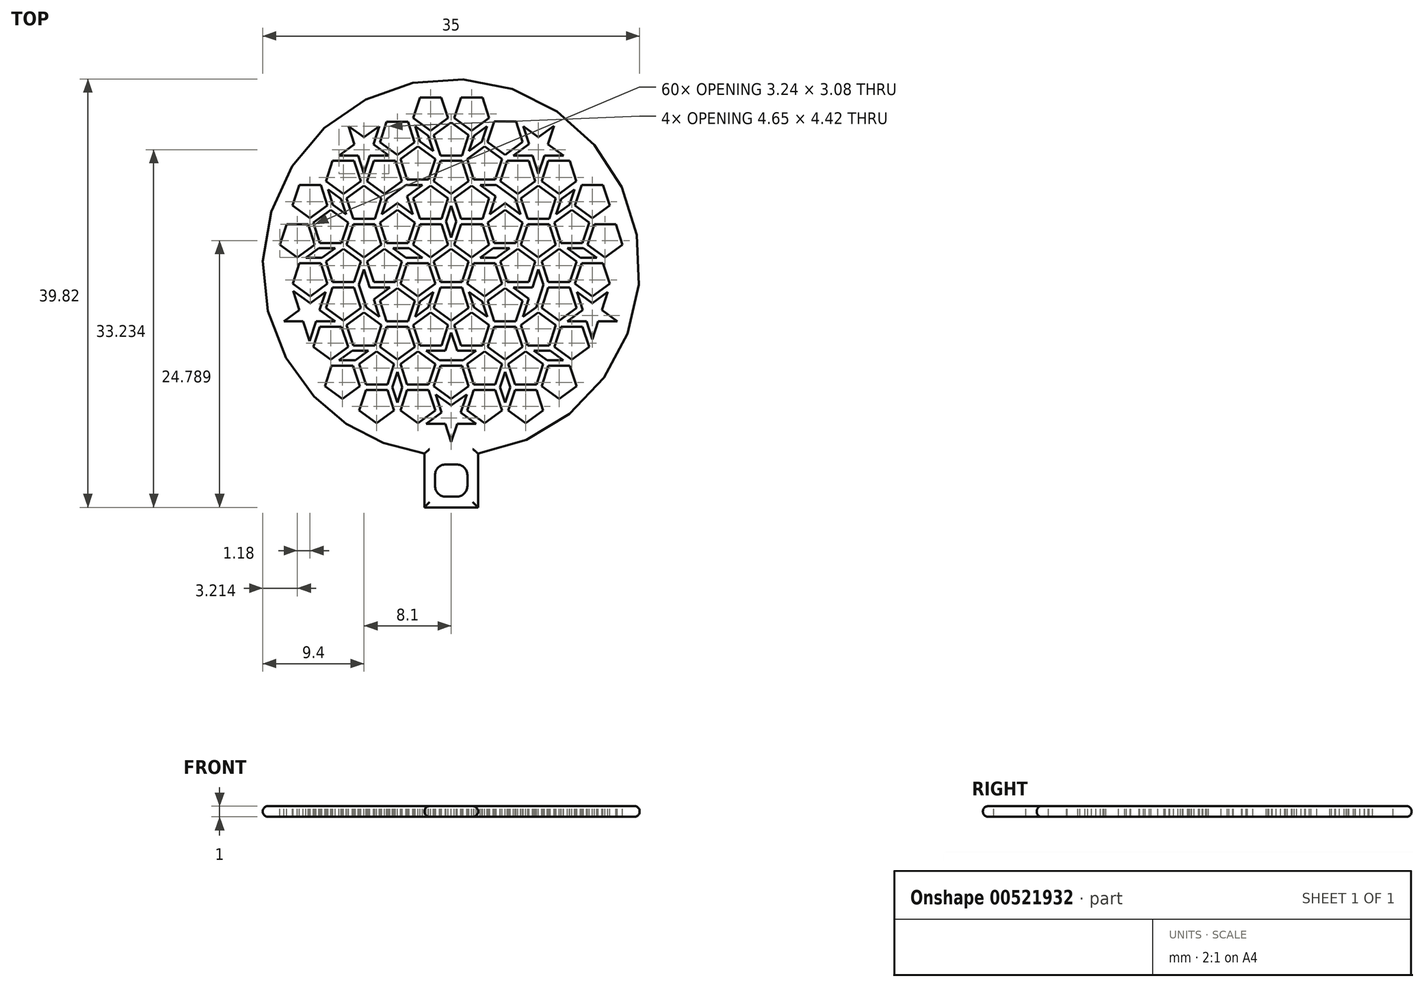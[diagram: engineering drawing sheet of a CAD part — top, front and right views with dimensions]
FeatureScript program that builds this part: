
annotation { "Feature Type Name" : "Feature", "Feature Type Description" : "" }
export const myFeature = defineFeature(function(context is Context, id is Id, definition is map)
    precondition{}
    {
        {
            var Q0;
            Q0=qCreatedBy(makeId("Top.planeOp"),FACE);
            var sketch = newSketch(context, id + "F0", { "sketchPlane" : qUnion([Q0])});
            skArc(sketch, "E0", {"start": v(2.5, -17.32) * mm, "mid": v(0, 17.5) * mm, "end": v(-2.5, -17.32) * mm});
            skLineSegment(sketch, "E1.bottom", {"start": v(2.5, -22.32) * mm, "end": v(-2.5, -22.32) * mm});
            skLineSegment(sketch, "E1.left", {"start": v(2.5, -22.32) * mm, "end": v(2.5, -17.32) * mm});
            skLineSegment(sketch, "E1.right", {"start": v(-2.5, -22.32) * mm, "end": v(-2.5, -17.32) * mm});
            skPoint(sketch, "E1.middle", {"position": v(0, -17.79) * mm});
            skPoint(sketch, "E2.orphan", {"position": v(2.5, -13.25) * mm});
            skPoint(sketch, "E3.orphan", {"position": v(-2.5, -13.25) * mm});
            skSolve(sketch);
        }
        {
            var Q0;
            Q0 = qSketchRegion(id + "F0", true);
            extrude(context, id + "F1", {"entities" : qUnion([Q0]), "depth" : 1 * mm, "offsetDistance" : 25 * mm});
        }
        {
            var Q0;
            Q0=makeQuery(id+"F1.opExtrude","CAP_EDGE",EDGE,{"disambiguationData":[OSD([sQuery(id+"F0.wireOp",EDGE,"E0")])],"isStart":false});
            var Q1;
            Q1=makeQuery(id+"F1.opExtrude","CAP_EDGE",EDGE,{"disambiguationData":[OSD([sQuery(id+"F0.wireOp",EDGE,"E0")])],"isStart":true});
            fillet(context, id + "F2", {"entities" : qUnion([Q0, Q1]), "radius" : 0.5 * mm, "tangentPropagation" : true, "allowEdgeOverflow" : false});
        }
        {
            var Q0;
            Q0=makeQuery(id+"F1.opExtrude","CAP_FACE",FACE,{"disambiguationData":[OSD([sQuery(id+"F0.wireOp",EDGE,"E0")])],"isStart":false});
            var sketch = newSketch(context, id + "F3", { "sketchPlane" : qUnion([Q0])});
            skCircle(sketch, "E4.cCircle", {"center": v(0, 0) * mm, "radius": 1.38 * mm, "construction": true});
            skLineSegment(sketch, "E4.0", {"start": v(0, 1.7) * mm, "end": v(1.62, 0.53) * mm});
            skLineSegment(sketch, "E4.1", {"start": v(1.62, 0.53) * mm, "end": v(1, -1.38) * mm});
            skLineSegment(sketch, "E4.2", {"start": v(1, -1.38) * mm, "end": v(-1, -1.38) * mm});
            skLineSegment(sketch, "E4.3", {"start": v(-1, -1.38) * mm, "end": v(-1.62, 0.53) * mm});
            skLineSegment(sketch, "E4.4", {"start": v(-1.62, 0.53) * mm, "end": v(0, 1.7) * mm});
            skPoint(sketch, "E4.0.midPoint", {"position": v(0.8, 1.11) * mm});
            skCircle(sketch, "E5.cCircle", {"center": v(1.91, 2.63) * mm, "radius": 1.38 * mm, "construction": true});
            skLineSegment(sketch, "E5.0", {"start": v(3.53, 2.1) * mm, "end": v(1.91, 0.93) * mm});
            skLineSegment(sketch, "E5.1", {"start": v(1.91, 0.93) * mm, "end": v(0.3, 2.1) * mm});
            skLineSegment(sketch, "E5.2", {"start": v(0.3, 2.1) * mm, "end": v(0.91, 4) * mm});
            skLineSegment(sketch, "E5.3", {"start": v(0.91, 4) * mm, "end": v(2.91, 4) * mm});
            skLineSegment(sketch, "E5.4", {"start": v(2.91, 4) * mm, "end": v(3.53, 2.1) * mm});
            skPoint(sketch, "E5.0.midPoint", {"position": v(2.72, 1.52) * mm});
            skCircle(sketch, "E6.cCircle", {"center": v(3.1, -1) * mm, "radius": 1.38 * mm, "construction": true});
            skLineSegment(sketch, "E6.0", {"start": v(4.1, 0.37) * mm, "end": v(4.71, -1.53) * mm});
            skLineSegment(sketch, "E6.1", {"start": v(4.71, -1.53) * mm, "end": v(3.1, -2.7) * mm});
            skLineSegment(sketch, "E6.2", {"start": v(3.1, -2.7) * mm, "end": v(1.48, -1.53) * mm});
            skLineSegment(sketch, "E6.3", {"start": v(1.48, -1.53) * mm, "end": v(2.1, 0.37) * mm});
            skLineSegment(sketch, "E6.4", {"start": v(2.1, 0.37) * mm, "end": v(4.1, 0.37) * mm});
            skPoint(sketch, "E6.0.midPoint", {"position": v(4.4, -0.58) * mm});
            skCircle(sketch, "E7.cCircle", {"center": v(0, -3.25) * mm, "radius": 1.38 * mm, "construction": true});
            skLineSegment(sketch, "E7.0", {"start": v(1.62, -3.78) * mm, "end": v(0, -4.95) * mm});
            skLineSegment(sketch, "E7.1", {"start": v(0, -4.95) * mm, "end": v(-1.62, -3.78) * mm});
            skLineSegment(sketch, "E7.2", {"start": v(-1.62, -3.78) * mm, "end": v(-1, -1.88) * mm});
            skLineSegment(sketch, "E7.3", {"start": v(-1, -1.88) * mm, "end": v(1, -1.88) * mm});
            skLineSegment(sketch, "E7.4", {"start": v(1, -1.88) * mm, "end": v(1.62, -3.78) * mm});
            skPoint(sketch, "E7.0.midPoint", {"position": v(0.8, -4.37) * mm});
            skCircle(sketch, "E8.cCircle", {"center": v(-3.1, -1) * mm, "radius": 1.38 * mm, "construction": true});
            skLineSegment(sketch, "E8.0", {"start": v(-4.1, 0.37) * mm, "end": v(-2.1, 0.37) * mm});
            skLineSegment(sketch, "E8.1", {"start": v(-2.1, 0.37) * mm, "end": v(-1.48, -1.53) * mm});
            skLineSegment(sketch, "E8.2", {"start": v(-1.48, -1.53) * mm, "end": v(-3.1, -2.7) * mm});
            skLineSegment(sketch, "E8.3", {"start": v(-3.1, -2.7) * mm, "end": v(-4.71, -1.53) * mm});
            skLineSegment(sketch, "E8.4", {"start": v(-4.71, -1.53) * mm, "end": v(-4.1, 0.37) * mm});
            skPoint(sketch, "E8.0.midPoint", {"position": v(-3.1, 0.37) * mm});
            skCircle(sketch, "E9.cCircle", {"center": v(-1.91, 2.63) * mm, "radius": 1.38 * mm, "construction": true});
            skLineSegment(sketch, "E9.0", {"start": v(-0.91, 4) * mm, "end": v(-0.3, 2.1) * mm});
            skLineSegment(sketch, "E9.1", {"start": v(-0.3, 2.1) * mm, "end": v(-1.91, 0.93) * mm});
            skLineSegment(sketch, "E9.2", {"start": v(-1.91, 0.93) * mm, "end": v(-3.53, 2.1) * mm});
            skLineSegment(sketch, "E9.3", {"start": v(-3.53, 2.1) * mm, "end": v(-2.91, 4) * mm});
            skLineSegment(sketch, "E9.4", {"start": v(-2.91, 4) * mm, "end": v(-0.91, 4) * mm});
            skPoint(sketch, "E9.0.midPoint", {"position": v(-0.6, 3.06) * mm});
            skLineSegment(sketch, "E10.0", {"start": v(5.42, 1.76) * mm, "end": v(4.2, 0.87) * mm});
            skLineSegment(sketch, "E10.1", {"start": v(4.2, 0.87) * mm, "end": v(2.68, 0.87) * mm});
            skLineSegment(sketch, "E10.2", {"start": v(2.68, 0.87) * mm, "end": v(3.9, 1.76) * mm});
            skLineSegment(sketch, "E10.3", {"start": v(3.9, 1.76) * mm, "end": v(5.42, 1.76) * mm});
            skPoint(sketch, "E10.0.midPoint", {"position": v(4.8, 1.32) * mm});
            skLineSegment(sketch, "E11", {"start": v(3.53, 2.1) * mm, "end": v(3.9, 1.76) * mm, "construction": true});
            skLineSegment(sketch, "E12", {"start": v(2.68, 0.87) * mm, "end": v(1.91, 0.93) * mm, "construction": true});
            skLineSegment(sketch, "E13", {"start": v(2.1, 0.37) * mm, "end": v(2.68, 0.87) * mm, "construction": true});
            skLineSegment(sketch, "E14", {"start": v(0.3, 2.1) * mm, "end": v(0, 1.7) * mm, "construction": true});
            skLineSegment(sketch, "E15", {"start": v(1.91, 0.93) * mm, "end": v(1.62, 0.53) * mm, "construction": true});
            skLineSegment(sketch, "E16", {"start": v(1.62, 0.53) * mm, "end": v(2.1, 0.37) * mm, "construction": true});
            skCircle(sketch, "E17.cCircle", {"center": v(5, 3.64) * mm, "radius": 1.38 * mm, "construction": true});
            skLineSegment(sketch, "E17.0", {"start": v(6.62, 4.16) * mm, "end": v(6, 2.26) * mm});
            skLineSegment(sketch, "E17.1", {"start": v(6, 2.26) * mm, "end": v(4, 2.26) * mm});
            skLineSegment(sketch, "E17.2", {"start": v(4, 2.26) * mm, "end": v(3.39, 4.16) * mm});
            skLineSegment(sketch, "E17.3", {"start": v(3.39, 4.16) * mm, "end": v(5, 5.34) * mm});
            skLineSegment(sketch, "E17.4", {"start": v(5, 5.34) * mm, "end": v(6.62, 4.16) * mm});
            skPoint(sketch, "E17.0.midPoint", {"position": v(6.31, 3.21) * mm});
            skLineSegment(sketch, "E18", {"start": v(2.91, 4) * mm, "end": v(3.39, 4.16) * mm, "construction": true});
            skCircle(sketch, "E19.cCircle", {"center": v(6.19, 0) * mm, "radius": 1.38 * mm, "construction": true});
            skLineSegment(sketch, "E19.0", {"start": v(7.8, 0.53) * mm, "end": v(7.19, -1.38) * mm});
            skLineSegment(sketch, "E19.1", {"start": v(7.19, -1.38) * mm, "end": v(5.19, -1.38) * mm});
            skLineSegment(sketch, "E19.2", {"start": v(5.19, -1.38) * mm, "end": v(4.57, 0.53) * mm});
            skLineSegment(sketch, "E19.3", {"start": v(4.57, 0.53) * mm, "end": v(6.19, 1.7) * mm});
            skLineSegment(sketch, "E19.4", {"start": v(6.19, 1.7) * mm, "end": v(7.8, 0.53) * mm});
            skPoint(sketch, "E19.0.midPoint", {"position": v(7.5, -0.43) * mm});
            skLineSegment(sketch, "E20", {"start": v(4.1, 0.37) * mm, "end": v(4.57, 0.53) * mm, "construction": true});
            skLineSegment(sketch, "E21.1", {"start": v(0, 2.75) * mm, "end": v(-0.47, 4.24) * mm});
            skLineSegment(sketch, "E22", {"start": v(-0.47, 4.24) * mm, "end": v(0, 5.7) * mm});
            skLineSegment(sketch, "E23", {"start": v(0, 5.7) * mm, "end": v(0.47, 4.24) * mm});
            skLineSegment(sketch, "E24", {"start": v(-0.3, 2.1) * mm, "end": v(0, 1.7) * mm, "construction": true});
            skLineSegment(sketch, "E25", {"start": v(5.42, 1.76) * mm, "end": v(6, 2.26) * mm, "construction": true});
            skLineSegment(sketch, "E26", {"start": v(5.42, 1.76) * mm, "end": v(6.19, 1.7) * mm, "construction": true});
            skLineSegment(sketch, "E27", {"start": v(0, 2.75) * mm, "end": v(-0.3, 2.1) * mm, "construction": true});
            skLineSegment(sketch, "E28", {"start": v(0.91, 4) * mm, "end": v(0.47, 4.24) * mm, "construction": true});
            skLineSegment(sketch, "E29", {"start": v(-0.47, 4.24) * mm, "end": v(-0.91, 4) * mm, "construction": true});
            skCircle(sketch, "E30.cCircle", {"center": v(1.91, 5.88) * mm, "radius": 1.38 * mm, "construction": true});
            skLineSegment(sketch, "E30.0", {"start": v(2.91, 4.5) * mm, "end": v(0.91, 4.5) * mm});
            skLineSegment(sketch, "E30.1", {"start": v(0.91, 4.5) * mm, "end": v(0.3, 6.41) * mm});
            skLineSegment(sketch, "E30.2", {"start": v(0.3, 6.41) * mm, "end": v(1.91, 7.59) * mm});
            skLineSegment(sketch, "E30.3", {"start": v(1.91, 7.59) * mm, "end": v(3.53, 6.41) * mm});
            skLineSegment(sketch, "E30.4", {"start": v(3.53, 6.41) * mm, "end": v(2.91, 4.5) * mm});
            skPoint(sketch, "E30.0.midPoint", {"position": v(1.91, 4.5) * mm});
            skLineSegment(sketch, "E31", {"start": v(0.91, 4.5) * mm, "end": v(0.91, 4) * mm, "construction": true});
            skLineSegment(sketch, "E32", {"start": v(2.91, 4.5) * mm, "end": v(2.91, 4) * mm, "construction": true});
            skLineSegment(sketch, "E33", {"start": v(0, 5.7) * mm, "end": v(0.3, 6.41) * mm, "construction": true});
            skCircle(sketch, "E34.cCircle", {"center": v(-1.91, 5.88) * mm, "radius": 1.38 * mm, "construction": true});
            skLineSegment(sketch, "E34.0", {"start": v(-0.3, 6.41) * mm, "end": v(-0.91, 4.5) * mm});
            skLineSegment(sketch, "E34.1", {"start": v(-0.91, 4.5) * mm, "end": v(-2.91, 4.5) * mm});
            skLineSegment(sketch, "E34.2", {"start": v(-2.91, 4.5) * mm, "end": v(-3.53, 6.41) * mm});
            skLineSegment(sketch, "E34.3", {"start": v(-3.53, 6.41) * mm, "end": v(-1.91, 7.59) * mm});
            skLineSegment(sketch, "E34.4", {"start": v(-1.91, 7.59) * mm, "end": v(-0.3, 6.41) * mm});
            skPoint(sketch, "E34.0.midPoint", {"position": v(-0.6, 5.46) * mm});
            skLineSegment(sketch, "E35", {"start": v(-0.3, 6.41) * mm, "end": v(0, 5.7) * mm, "construction": true});
            skLineSegment(sketch, "E36", {"start": v(-0.91, 4.5) * mm, "end": v(-0.91, 4) * mm, "construction": true});
            skLineSegment(sketch, "E37", {"start": v(-2.91, 4.5) * mm, "end": v(-2.91, 4) * mm, "construction": true});
            skLineSegment(sketch, "E38", {"start": v(-2.68, 0.87) * mm, "end": v(-3.9, 1.76) * mm});
            skLineSegment(sketch, "E39", {"start": v(-3.9, 1.76) * mm, "end": v(-5.42, 1.76) * mm});
            skLineSegment(sketch, "E40", {"start": v(-5.42, 1.76) * mm, "end": v(-4.2, 0.87) * mm});
            skLineSegment(sketch, "E41", {"start": v(-4.2, 0.87) * mm, "end": v(-2.68, 0.87) * mm});
            skLineSegment(sketch, "E42", {"start": v(-2.68, 0.87) * mm, "end": v(-1.91, 0.93) * mm, "construction": true});
            skLineSegment(sketch, "E43", {"start": v(-2.68, 0.87) * mm, "end": v(-2.1, 0.37) * mm, "construction": true});
            skLineSegment(sketch, "E44", {"start": v(-4.2, 0.87) * mm, "end": v(-4.1, 0.37) * mm, "construction": true});
            skLineSegment(sketch, "E45", {"start": v(-3.9, 1.76) * mm, "end": v(-3.53, 2.1) * mm, "construction": true});
            skLineSegment(sketch, "E46", {"start": v(0, 2.75) * mm, "end": v(0.47, 4.24) * mm});
            skLineSegment(sketch, "E47", {"start": v(0.3, 2.1) * mm, "end": v(0, 2.75) * mm, "construction": true});
            skCircle(sketch, "E48.cCircle", {"center": v(-5, 3.64) * mm, "radius": 1.38 * mm, "construction": true});
            skLineSegment(sketch, "E48.0", {"start": v(-5, 5.34) * mm, "end": v(-3.39, 4.16) * mm});
            skLineSegment(sketch, "E48.1", {"start": v(-3.39, 4.16) * mm, "end": v(-4, 2.26) * mm});
            skLineSegment(sketch, "E48.2", {"start": v(-4, 2.26) * mm, "end": v(-6, 2.26) * mm});
            skLineSegment(sketch, "E48.3", {"start": v(-6, 2.26) * mm, "end": v(-6.62, 4.16) * mm});
            skLineSegment(sketch, "E48.4", {"start": v(-6.62, 4.16) * mm, "end": v(-5, 5.34) * mm});
            skPoint(sketch, "E48.0.midPoint", {"position": v(-4.2, 4.75) * mm});
            skLineSegment(sketch, "E49", {"start": v(-3.39, 4.16) * mm, "end": v(-2.91, 4) * mm, "construction": true});
            skLineSegment(sketch, "E50", {"start": v(-3.53, 2.1) * mm, "end": v(-4, 2.26) * mm, "construction": true});
            skCircle(sketch, "E51.cCircle", {"center": v(-6.19, 0) * mm, "radius": 1.38 * mm, "construction": true});
            skLineSegment(sketch, "E51.0", {"start": v(-6.19, 1.7) * mm, "end": v(-4.57, 0.53) * mm});
            skLineSegment(sketch, "E51.1", {"start": v(-4.57, 0.53) * mm, "end": v(-5.19, -1.38) * mm});
            skLineSegment(sketch, "E51.2", {"start": v(-5.19, -1.38) * mm, "end": v(-7.19, -1.38) * mm});
            skLineSegment(sketch, "E51.3", {"start": v(-7.19, -1.38) * mm, "end": v(-7.8, 0.53) * mm});
            skLineSegment(sketch, "E51.4", {"start": v(-7.8, 0.53) * mm, "end": v(-6.19, 1.7) * mm});
            skPoint(sketch, "E51.0.midPoint", {"position": v(-5.38, 1.11) * mm});
            skLineSegment(sketch, "E52", {"start": v(-4.57, 0.53) * mm, "end": v(-4.1, 0.37) * mm, "construction": true});
            skLineSegment(sketch, "E53", {"start": v(-4.71, -1.53) * mm, "end": v(-5.19, -1.38) * mm, "construction": true});
            skLineSegment(sketch, "E54", {"start": v(-6.19, 1.7) * mm, "end": v(-5.42, 1.76) * mm, "construction": true});
            skLineSegment(sketch, "E55", {"start": v(-6, 2.26) * mm, "end": v(-5.42, 1.76) * mm, "construction": true});
            skLineSegment(sketch, "E56", {"start": v(-2.88, -3.17) * mm, "end": v(-1.66, -2.28) * mm});
            skLineSegment(sketch, "E57", {"start": v(-1.66, -2.28) * mm, "end": v(-2.12, -3.72) * mm});
            skLineSegment(sketch, "E58", {"start": v(-2.12, -3.72) * mm, "end": v(-3.35, -4.6) * mm});
            skLineSegment(sketch, "E59", {"start": v(-3.35, -4.6) * mm, "end": v(-2.88, -3.17) * mm});
            skLineSegment(sketch, "E60", {"start": v(-1.48, -1.53) * mm, "end": v(-1.66, -2.28) * mm, "construction": true});
            skLineSegment(sketch, "E61", {"start": v(-1, -1.88) * mm, "end": v(-1.66, -2.28) * mm, "construction": true});
            skLineSegment(sketch, "E62", {"start": v(-1.62, -3.78) * mm, "end": v(-2.12, -3.72) * mm, "construction": true});
            skLineSegment(sketch, "E63", {"start": v(-2.88, -3.17) * mm, "end": v(-3.1, -2.7) * mm, "construction": true});
            skLineSegment(sketch, "E64", {"start": v(2.12, -3.72) * mm, "end": v(1.66, -2.28) * mm});
            skLineSegment(sketch, "E65", {"start": v(1.66, -2.28) * mm, "end": v(2.88, -3.17) * mm});
            skLineSegment(sketch, "E66", {"start": v(2.88, -3.17) * mm, "end": v(3.35, -4.6) * mm});
            skLineSegment(sketch, "E67", {"start": v(3.35, -4.6) * mm, "end": v(2.12, -3.72) * mm});
            skLineSegment(sketch, "E68", {"start": v(1.66, -2.28) * mm, "end": v(1.48, -1.53) * mm, "construction": true});
            skLineSegment(sketch, "E69", {"start": v(1.66, -2.28) * mm, "end": v(1, -1.88) * mm, "construction": true});
            skCircle(sketch, "E70.cCircle", {"center": v(5, -3.64) * mm, "radius": 1.38 * mm, "construction": true});
            skLineSegment(sketch, "E70.0", {"start": v(6.62, -3.11) * mm, "end": v(6, -5.01) * mm});
            skLineSegment(sketch, "E70.1", {"start": v(6, -5.01) * mm, "end": v(4, -5.01) * mm});
            skLineSegment(sketch, "E70.2", {"start": v(4, -5.01) * mm, "end": v(3.39, -3.11) * mm});
            skLineSegment(sketch, "E70.3", {"start": v(3.39, -3.11) * mm, "end": v(5, -1.94) * mm});
            skLineSegment(sketch, "E70.4", {"start": v(5, -1.94) * mm, "end": v(6.62, -3.11) * mm});
            skPoint(sketch, "E70.0.midPoint", {"position": v(6.31, -4.06) * mm});
            skCircle(sketch, "E71.cCircle", {"center": v(1.91, -5.88) * mm, "radius": 1.38 * mm, "construction": true});
            skLineSegment(sketch, "E71.0", {"start": v(1.91, -4.18) * mm, "end": v(3.53, -5.36) * mm});
            skLineSegment(sketch, "E71.1", {"start": v(3.53, -5.36) * mm, "end": v(2.91, -7.26) * mm});
            skLineSegment(sketch, "E71.2", {"start": v(2.91, -7.26) * mm, "end": v(0.91, -7.26) * mm});
            skLineSegment(sketch, "E71.3", {"start": v(0.91, -7.26) * mm, "end": v(0.3, -5.36) * mm});
            skLineSegment(sketch, "E71.4", {"start": v(0.3, -5.36) * mm, "end": v(1.91, -4.18) * mm});
            skPoint(sketch, "E71.0.midPoint", {"position": v(2.72, -4.77) * mm});
            skCircle(sketch, "E72.cCircle", {"center": v(-1.91, -5.88) * mm, "radius": 1.38 * mm, "construction": true});
            skLineSegment(sketch, "E72.0", {"start": v(-0.3, -5.36) * mm, "end": v(-0.91, -7.26) * mm});
            skLineSegment(sketch, "E72.1", {"start": v(-0.91, -7.26) * mm, "end": v(-2.91, -7.26) * mm});
            skLineSegment(sketch, "E72.2", {"start": v(-2.91, -7.26) * mm, "end": v(-3.53, -5.36) * mm});
            skLineSegment(sketch, "E72.3", {"start": v(-3.53, -5.36) * mm, "end": v(-1.91, -4.18) * mm});
            skLineSegment(sketch, "E72.4", {"start": v(-1.91, -4.18) * mm, "end": v(-0.3, -5.36) * mm});
            skCircle(sketch, "E73.cCircle", {"center": v(-5, -3.64) * mm, "radius": 1.38 * mm, "construction": true});
            skLineSegment(sketch, "E73.0", {"start": v(-3.39, -3.11) * mm, "end": v(-4, -5.01) * mm});
            skLineSegment(sketch, "E73.1", {"start": v(-4, -5.01) * mm, "end": v(-6, -5.01) * mm});
            skLineSegment(sketch, "E73.2", {"start": v(-6, -5.01) * mm, "end": v(-6.62, -3.11) * mm});
            skLineSegment(sketch, "E73.3", {"start": v(-6.62, -3.11) * mm, "end": v(-5, -1.94) * mm});
            skLineSegment(sketch, "E73.4", {"start": v(-5, -1.94) * mm, "end": v(-3.39, -3.11) * mm});
            skPoint(sketch, "E73.0.midPoint", {"position": v(-3.7, -4.06) * mm});
            skLineSegment(sketch, "E74", {"start": v(3.39, -3.11) * mm, "end": v(3.1, -2.7) * mm, "construction": true});
            skLineSegment(sketch, "E75", {"start": v(0.3, -5.36) * mm, "end": v(0, -4.95) * mm, "construction": true});
            skLineSegment(sketch, "E76", {"start": v(-0.3, -5.36) * mm, "end": v(0, -4.95) * mm, "construction": true});
            skLineSegment(sketch, "E77", {"start": v(-5, -1.94) * mm, "end": v(-4.71, -1.53) * mm, "construction": true});
            skLineSegment(sketch, "E78", {"start": v(-3.35, -4.6) * mm, "end": v(-4, -5.01) * mm, "construction": true});
            skLineSegment(sketch, "E79", {"start": v(-3.35, -4.6) * mm, "end": v(-3.53, -5.36) * mm, "construction": true});
            skLineSegment(sketch, "E80", {"start": v(-2.12, -3.72) * mm, "end": v(-1.91, -4.18) * mm, "construction": true});
            skLineSegment(sketch, "E81", {"start": v(-3.39, -3.11) * mm, "end": v(-2.88, -3.17) * mm, "construction": true});
            skLineSegment(sketch, "E82", {"start": v(1.62, -3.78) * mm, "end": v(2.12, -3.72) * mm, "construction": true});
            skLineSegment(sketch, "E83", {"start": v(3.1, -2.7) * mm, "end": v(2.88, -3.17) * mm, "construction": true});
            skLineSegment(sketch, "E84", {"start": v(2.88, -3.17) * mm, "end": v(3.39, -3.11) * mm, "construction": true});
            skLineSegment(sketch, "E85", {"start": v(1.91, -4.18) * mm, "end": v(2.12, -3.72) * mm, "construction": true});
            skCircle(sketch, "E86.cCircle", {"center": v(10.01, 0) * mm, "radius": 1.38 * mm, "construction": true});
            skLineSegment(sketch, "E86.0", {"start": v(11.63, 0.53) * mm, "end": v(11.01, -1.38) * mm});
            skLineSegment(sketch, "E86.1", {"start": v(11.01, -1.38) * mm, "end": v(9.01, -1.38) * mm});
            skLineSegment(sketch, "E86.2", {"start": v(9.01, -1.38) * mm, "end": v(8.4, 0.53) * mm});
            skLineSegment(sketch, "E86.3", {"start": v(8.4, 0.53) * mm, "end": v(10.01, 1.7) * mm});
            skLineSegment(sketch, "E86.4", {"start": v(10.01, 1.7) * mm, "end": v(11.63, 0.53) * mm});
            skPoint(sketch, "E86.0.midPoint", {"position": v(11.32, -0.43) * mm});
            skCircle(sketch, "E87.cCircle", {"center": v(8.1, -5.88) * mm, "radius": 1.38 * mm, "construction": true});
            skLineSegment(sketch, "E87.0", {"start": v(9.1, -7.26) * mm, "end": v(7.1, -7.26) * mm});
            skLineSegment(sketch, "E87.1", {"start": v(7.1, -7.26) * mm, "end": v(6.48, -5.36) * mm});
            skLineSegment(sketch, "E87.2", {"start": v(6.48, -5.36) * mm, "end": v(8.1, -4.18) * mm});
            skLineSegment(sketch, "E87.3", {"start": v(8.1, -4.18) * mm, "end": v(9.72, -5.36) * mm});
            skLineSegment(sketch, "E87.4", {"start": v(9.72, -5.36) * mm, "end": v(9.1, -7.26) * mm});
            skPoint(sketch, "E87.0.midPoint", {"position": v(8.1, -7.26) * mm});
            skCircle(sketch, "E88.cCircle", {"center": v(5, -6.89) * mm, "radius": 1.38 * mm, "construction": true});
            skLineSegment(sketch, "E88.0", {"start": v(6.62, -7.42) * mm, "end": v(5, -8.6) * mm});
            skLineSegment(sketch, "E88.1", {"start": v(5, -8.6) * mm, "end": v(3.39, -7.42) * mm});
            skLineSegment(sketch, "E88.2", {"start": v(3.39, -7.42) * mm, "end": v(4, -5.51) * mm});
            skLineSegment(sketch, "E88.3", {"start": v(4, -5.51) * mm, "end": v(6, -5.51) * mm});
            skLineSegment(sketch, "E88.4", {"start": v(6, -5.51) * mm, "end": v(6.62, -7.42) * mm});
            skPoint(sketch, "E88.0.midPoint", {"position": v(5.81, -8) * mm});
            skCircle(sketch, "E89.cCircle", {"center": v(8.1, 2.63) * mm, "radius": 1.38 * mm, "construction": true});
            skLineSegment(sketch, "E89.0", {"start": v(9.72, 2.1) * mm, "end": v(8.1, 0.93) * mm});
            skLineSegment(sketch, "E89.1", {"start": v(8.1, 0.93) * mm, "end": v(6.48, 2.1) * mm});
            skLineSegment(sketch, "E89.2", {"start": v(6.48, 2.1) * mm, "end": v(7.1, 4) * mm});
            skLineSegment(sketch, "E89.3", {"start": v(7.1, 4) * mm, "end": v(9.1, 4) * mm});
            skLineSegment(sketch, "E89.4", {"start": v(9.1, 4) * mm, "end": v(9.72, 2.1) * mm});
            skPoint(sketch, "E89.0.midPoint", {"position": v(8.9, 1.52) * mm});
            skLineSegment(sketch, "E90", {"start": v(6.48, 2.1) * mm, "end": v(6.19, 1.7) * mm, "construction": true});
            skLineSegment(sketch, "E91", {"start": v(10.01, 1.7) * mm, "end": v(9.72, 2.1) * mm, "construction": true});
            skLineSegment(sketch, "E92", {"start": v(4, -5.51) * mm, "end": v(3.53, -5.36) * mm, "construction": true});
            skLineSegment(sketch, "E93", {"start": v(6.48, -5.36) * mm, "end": v(6, -5.51) * mm, "construction": true});
            skCircle(sketch, "E94.cCircle", {"center": v(10.01, -3.25) * mm, "radius": 1.38 * mm, "construction": true});
            skLineSegment(sketch, "E94.0", {"start": v(11.01, -1.88) * mm, "end": v(11.63, -3.78) * mm});
            skLineSegment(sketch, "E94.1", {"start": v(11.63, -3.78) * mm, "end": v(10.01, -4.95) * mm});
            skLineSegment(sketch, "E94.2", {"start": v(10.01, -4.95) * mm, "end": v(8.4, -3.78) * mm});
            skLineSegment(sketch, "E94.3", {"start": v(8.4, -3.78) * mm, "end": v(9.01, -1.88) * mm});
            skLineSegment(sketch, "E94.4", {"start": v(9.01, -1.88) * mm, "end": v(11.01, -1.88) * mm});
            skPoint(sketch, "E94.0.midPoint", {"position": v(11.32, -2.83) * mm});
            skLineSegment(sketch, "E95", {"start": v(11.01, -1.38) * mm, "end": v(11.01, -1.88) * mm, "construction": true});
            skLineSegment(sketch, "E96", {"start": v(6.66, -4.6) * mm, "end": v(7.21, -2.92) * mm});
            skLineSegment(sketch, "E97", {"start": v(7.21, -2.92) * mm, "end": v(5.77, -1.88) * mm});
            skLineSegment(sketch, "E98", {"start": v(5.77, -1.88) * mm, "end": v(7.55, -1.88) * mm});
            skLineSegment(sketch, "E99", {"start": v(7.55, -1.88) * mm, "end": v(8.1, -0.19) * mm});
            skLineSegment(sketch, "E100", {"start": v(8.1, -0.19) * mm, "end": v(8.57, -1.63) * mm});
            skLineSegment(sketch, "E101", {"start": v(8.57, -1.63) * mm, "end": v(7.89, -3.72) * mm});
            skLineSegment(sketch, "E102", {"start": v(7.89, -3.72) * mm, "end": v(6.66, -4.6) * mm});
            skCircle(sketch, "E103.cCircle", {"center": v(-8.1, 2.63) * mm, "radius": 1.38 * mm, "construction": true});
            skLineSegment(sketch, "E103.0", {"start": v(-6.48, 2.1) * mm, "end": v(-8.1, 0.93) * mm});
            skLineSegment(sketch, "E103.1", {"start": v(-8.1, 0.93) * mm, "end": v(-9.72, 2.1) * mm});
            skLineSegment(sketch, "E103.2", {"start": v(-9.72, 2.1) * mm, "end": v(-9.1, 4) * mm});
            skLineSegment(sketch, "E103.3", {"start": v(-9.1, 4) * mm, "end": v(-7.1, 4) * mm});
            skLineSegment(sketch, "E103.4", {"start": v(-7.1, 4) * mm, "end": v(-6.48, 2.1) * mm});
            skPoint(sketch, "E103.0.midPoint", {"position": v(-7.3, 1.52) * mm});
            skCircle(sketch, "E104.cCircle", {"center": v(0, 8.51) * mm, "radius": 1.38 * mm, "construction": true});
            skLineSegment(sketch, "E104.0", {"start": v(1.62, 7.99) * mm, "end": v(0, 6.81) * mm});
            skLineSegment(sketch, "E104.1", {"start": v(0, 6.81) * mm, "end": v(-1.62, 7.99) * mm});
            skLineSegment(sketch, "E104.2", {"start": v(-1.62, 7.99) * mm, "end": v(-1, 9.9) * mm});
            skLineSegment(sketch, "E104.3", {"start": v(-1, 9.9) * mm, "end": v(1, 9.9) * mm});
            skLineSegment(sketch, "E104.4", {"start": v(1, 9.9) * mm, "end": v(1.62, 7.99) * mm});
            skPoint(sketch, "E104.0.midPoint", {"position": v(0.8, 7.4) * mm});
            skCircle(sketch, "E105.cCircle", {"center": v(3.1, 9.52) * mm, "radius": 1.38 * mm, "construction": true});
            skLineSegment(sketch, "E105.0", {"start": v(4.71, 10.05) * mm, "end": v(4.1, 8.14) * mm});
            skLineSegment(sketch, "E105.1", {"start": v(4.1, 8.14) * mm, "end": v(2.1, 8.14) * mm});
            skLineSegment(sketch, "E105.2", {"start": v(2.1, 8.14) * mm, "end": v(1.47, 10.05) * mm});
            skLineSegment(sketch, "E105.3", {"start": v(1.47, 10.05) * mm, "end": v(3.1, 11.22) * mm});
            skLineSegment(sketch, "E105.4", {"start": v(3.1, 11.22) * mm, "end": v(4.71, 10.05) * mm});
            skPoint(sketch, "E105.0.midPoint", {"position": v(4.4, 9.1) * mm});
            skCircle(sketch, "E106.cCircle", {"center": v(-3.1, 9.52) * mm, "radius": 1.38 * mm, "construction": true});
            skLineSegment(sketch, "E106.0", {"start": v(-2.1, 8.14) * mm, "end": v(-4.1, 8.14) * mm});
            skLineSegment(sketch, "E106.1", {"start": v(-4.1, 8.14) * mm, "end": v(-4.71, 10.05) * mm});
            skLineSegment(sketch, "E106.2", {"start": v(-4.71, 10.05) * mm, "end": v(-3.1, 11.22) * mm});
            skLineSegment(sketch, "E106.3", {"start": v(-3.1, 11.22) * mm, "end": v(-1.48, 10.05) * mm});
            skLineSegment(sketch, "E106.4", {"start": v(-1.48, 10.05) * mm, "end": v(-2.1, 8.14) * mm});
            skPoint(sketch, "E106.0.midPoint", {"position": v(-3.1, 8.14) * mm});
            skCircle(sketch, "E107.cCircle", {"center": v(-8.1, 5.88) * mm, "radius": 1.38 * mm, "construction": true});
            skLineSegment(sketch, "E107.0", {"start": v(-6.48, 6.41) * mm, "end": v(-7.1, 4.5) * mm});
            skLineSegment(sketch, "E107.1", {"start": v(-7.1, 4.5) * mm, "end": v(-9.1, 4.5) * mm});
            skLineSegment(sketch, "E107.2", {"start": v(-9.1, 4.5) * mm, "end": v(-9.72, 6.41) * mm});
            skLineSegment(sketch, "E107.3", {"start": v(-9.72, 6.41) * mm, "end": v(-8.1, 7.59) * mm});
            skLineSegment(sketch, "E107.4", {"start": v(-8.1, 7.59) * mm, "end": v(-6.48, 6.41) * mm});
            skPoint(sketch, "E107.0.midPoint", {"position": v(-6.8, 5.46) * mm});
            skCircle(sketch, "E108.cCircle", {"center": v(-10.01, 0) * mm, "radius": 1.38 * mm, "construction": true});
            skLineSegment(sketch, "E108.0", {"start": v(-8.4, 0.53) * mm, "end": v(-9.01, -1.38) * mm});
            skLineSegment(sketch, "E108.1", {"start": v(-9.01, -1.38) * mm, "end": v(-11.01, -1.38) * mm});
            skLineSegment(sketch, "E108.2", {"start": v(-11.01, -1.38) * mm, "end": v(-11.63, 0.53) * mm});
            skLineSegment(sketch, "E108.3", {"start": v(-11.63, 0.53) * mm, "end": v(-10.01, 1.7) * mm});
            skLineSegment(sketch, "E108.4", {"start": v(-10.01, 1.7) * mm, "end": v(-8.4, 0.53) * mm});
            skPoint(sketch, "E108.0.midPoint", {"position": v(-8.7, -0.43) * mm});
            skLineSegment(sketch, "E109", {"start": v(-6.48, 2.1) * mm, "end": v(-6.19, 1.7) * mm, "construction": true});
            skLineSegment(sketch, "E110", {"start": v(0, 6.81) * mm, "end": v(-0.3, 6.41) * mm, "construction": true});
            skLineSegment(sketch, "E111", {"start": v(-7.1, 4.5) * mm, "end": v(-7.1, 4) * mm, "construction": true});
            skLineSegment(sketch, "E112", {"start": v(-2.1, 8.14) * mm, "end": v(-1.62, 7.99) * mm, "construction": true});
            skLineSegment(sketch, "E113", {"start": v(-8.4, 0.53) * mm, "end": v(-8.1, 0.93) * mm, "construction": true});
            skLineSegment(sketch, "E114", {"start": v(1.62, 7.99) * mm, "end": v(2.1, 8.14) * mm, "construction": true});
            skCircle(sketch, "E115.cCircle", {"center": v(-10.01, -3.25) * mm, "radius": 1.38 * mm, "construction": true});
            skLineSegment(sketch, "E115.0", {"start": v(-9.01, -1.88) * mm, "end": v(-8.4, -3.78) * mm});
            skLineSegment(sketch, "E115.1", {"start": v(-8.4, -3.78) * mm, "end": v(-10.01, -4.95) * mm});
            skLineSegment(sketch, "E115.2", {"start": v(-10.01, -4.95) * mm, "end": v(-11.63, -3.78) * mm});
            skLineSegment(sketch, "E115.3", {"start": v(-11.63, -3.78) * mm, "end": v(-11.01, -1.88) * mm});
            skLineSegment(sketch, "E115.4", {"start": v(-11.01, -1.88) * mm, "end": v(-9.01, -1.88) * mm});
            skPoint(sketch, "E115.0.midPoint", {"position": v(-8.7, -2.83) * mm});
            skCircle(sketch, "E116.cCircle", {"center": v(8.1, 5.88) * mm, "radius": 1.38 * mm, "construction": true});
            skLineSegment(sketch, "E116.0", {"start": v(9.1, 4.5) * mm, "end": v(7.1, 4.5) * mm});
            skLineSegment(sketch, "E116.1", {"start": v(7.1, 4.5) * mm, "end": v(6.48, 6.4) * mm});
            skLineSegment(sketch, "E116.2", {"start": v(6.48, 6.4) * mm, "end": v(8.1, 7.58) * mm});
            skLineSegment(sketch, "E116.3", {"start": v(8.1, 7.58) * mm, "end": v(9.72, 6.4) * mm});
            skLineSegment(sketch, "E116.4", {"start": v(9.72, 6.4) * mm, "end": v(9.1, 4.5) * mm});
            skPoint(sketch, "E116.0.midPoint", {"position": v(8.1, 4.5) * mm});
            skCircle(sketch, "E117.cCircle", {"center": v(6.19, 8.51) * mm, "radius": 1.38 * mm, "construction": true});
            skLineSegment(sketch, "E117.0", {"start": v(7.8, 7.99) * mm, "end": v(6.19, 6.81) * mm});
            skLineSegment(sketch, "E117.1", {"start": v(6.19, 6.81) * mm, "end": v(4.57, 7.99) * mm});
            skLineSegment(sketch, "E117.2", {"start": v(4.57, 7.99) * mm, "end": v(5.19, 9.9) * mm});
            skLineSegment(sketch, "E117.3", {"start": v(5.19, 9.9) * mm, "end": v(7.19, 9.9) * mm});
            skLineSegment(sketch, "E117.4", {"start": v(7.19, 9.9) * mm, "end": v(7.8, 7.99) * mm});
            skPoint(sketch, "E117.0.midPoint", {"position": v(7, 7.4) * mm});
            skCircle(sketch, "E118.cCircle", {"center": v(-6.19, 8.51) * mm, "radius": 1.38 * mm, "construction": true});
            skLineSegment(sketch, "E118.0", {"start": v(-4.57, 7.99) * mm, "end": v(-6.19, 6.81) * mm});
            skLineSegment(sketch, "E118.1", {"start": v(-6.19, 6.81) * mm, "end": v(-7.8, 7.99) * mm});
            skLineSegment(sketch, "E118.2", {"start": v(-7.8, 7.99) * mm, "end": v(-7.19, 9.9) * mm});
            skLineSegment(sketch, "E118.3", {"start": v(-7.19, 9.9) * mm, "end": v(-5.19, 9.9) * mm});
            skLineSegment(sketch, "E118.4", {"start": v(-5.19, 9.9) * mm, "end": v(-4.57, 7.99) * mm});
            skPoint(sketch, "E118.0.midPoint", {"position": v(-5.38, 7.4) * mm});
            skLineSegment(sketch, "E119", {"start": v(-4.1, 8.14) * mm, "end": v(-4.57, 7.99) * mm, "construction": true});
            skLineSegment(sketch, "E120", {"start": v(4.1, 8.14) * mm, "end": v(4.57, 7.99) * mm, "construction": true});
            skLineSegment(sketch, "E121", {"start": v(-11.01, -1.88) * mm, "end": v(-11.01, -1.38) * mm, "construction": true});
            skLineSegment(sketch, "E122", {"start": v(-8.1, 7.59) * mm, "end": v(-7.8, 7.99) * mm, "construction": true});
            skLineSegment(sketch, "E123", {"start": v(6.19, 6.81) * mm, "end": v(6.48, 6.4) * mm, "construction": true});
            skSolve(sketch);
        }
        {
            var Q0;
            Q0 = qSketchRegion(id + "F3", true);
            extrude(context, id + "F4", {"entities" : qUnion([Q0]), "operationType" : NewBodyOperationType.REMOVE, "endBound" : BoundingType.THROUGH_ALL, "oppositeDirection" : true, "depth" : 25 * mm, "offsetDistance" : 25 * mm});
        }
        {
            var Q0;
            Q0=makeQuery(id+"F1.opExtrude","CAP_FACE",FACE,{"disambiguationData":[OSD([sQuery(id+"F0.wireOp",EDGE,"E0")])],"isStart":false});
            var sketch = newSketch(context, id + "F5", { "sketchPlane" : qUnion([Q0])});
            skCircle(sketch, "E124.cCircle", {"center": v(-8.1, -5.88) * mm, "radius": 1.38 * mm, "construction": true});
            skLineSegment(sketch, "E124.0", {"start": v(-6.48, -5.36) * mm, "end": v(-7.1, -7.26) * mm});
            skLineSegment(sketch, "E124.1", {"start": v(-7.1, -7.26) * mm, "end": v(-9.1, -7.26) * mm});
            skLineSegment(sketch, "E124.2", {"start": v(-9.1, -7.26) * mm, "end": v(-9.72, -5.36) * mm});
            skLineSegment(sketch, "E124.3", {"start": v(-9.72, -5.36) * mm, "end": v(-8.1, -4.18) * mm});
            skLineSegment(sketch, "E124.4", {"start": v(-8.1, -4.18) * mm, "end": v(-6.48, -5.36) * mm});
            skPoint(sketch, "E124.0.midPoint", {"position": v(-6.8, -6.3) * mm});
            skLineSegment(sketch, "E125", {"start": v(-8.1, -4.18) * mm, "end": v(-8.4, -3.78) * mm, "construction": true});
            skCircle(sketch, "E126.cCircle", {"center": v(-5, -6.89) * mm, "radius": 1.38 * mm, "construction": true});
            skLineSegment(sketch, "E126.0", {"start": v(-3.39, -7.42) * mm, "end": v(-5, -8.6) * mm});
            skLineSegment(sketch, "E126.1", {"start": v(-5, -8.6) * mm, "end": v(-6.62, -7.42) * mm});
            skLineSegment(sketch, "E126.2", {"start": v(-6.62, -7.42) * mm, "end": v(-6, -5.51) * mm});
            skLineSegment(sketch, "E126.3", {"start": v(-6, -5.51) * mm, "end": v(-4, -5.51) * mm});
            skLineSegment(sketch, "E126.4", {"start": v(-4, -5.51) * mm, "end": v(-3.39, -7.42) * mm});
            skPoint(sketch, "E126.0.midPoint", {"position": v(-4.2, -8) * mm});
            skLineSegment(sketch, "E127", {"start": v(-6, -5.51) * mm, "end": v(-6.48, -5.36) * mm, "construction": true});
            skCircle(sketch, "E128.cCircle", {"center": v(-3.1, -9.52) * mm, "radius": 1.38 * mm, "construction": true});
            skLineSegment(sketch, "E128.0", {"start": v(-1.48, -9) * mm, "end": v(-2.1, -10.9) * mm});
            skLineSegment(sketch, "E128.1", {"start": v(-2.1, -10.9) * mm, "end": v(-4.1, -10.9) * mm});
            skLineSegment(sketch, "E128.2", {"start": v(-4.1, -10.9) * mm, "end": v(-4.71, -9) * mm});
            skLineSegment(sketch, "E128.3", {"start": v(-4.71, -9) * mm, "end": v(-3.1, -7.82) * mm});
            skLineSegment(sketch, "E128.4", {"start": v(-3.1, -7.82) * mm, "end": v(-1.48, -9) * mm});
            skPoint(sketch, "E128.0.midPoint", {"position": v(-1.78, -9.95) * mm});
            skLineSegment(sketch, "E129", {"start": v(-3.39, -7.42) * mm, "end": v(-3.1, -7.82) * mm, "construction": true});
            skCircle(sketch, "E130.cCircle", {"center": v(0, -10.53) * mm, "radius": 1.38 * mm, "construction": true});
            skLineSegment(sketch, "E130.0", {"start": v(1.62, -11.05) * mm, "end": v(0, -12.23) * mm});
            skLineSegment(sketch, "E130.1", {"start": v(0, -12.23) * mm, "end": v(-1.62, -11.05) * mm});
            skLineSegment(sketch, "E130.2", {"start": v(-1.62, -11.05) * mm, "end": v(-1, -9.15) * mm});
            skLineSegment(sketch, "E130.3", {"start": v(-1, -9.15) * mm, "end": v(1, -9.15) * mm});
            skLineSegment(sketch, "E130.4", {"start": v(1, -9.15) * mm, "end": v(1.62, -11.05) * mm});
            skPoint(sketch, "E130.0.midPoint", {"position": v(0.8, -11.64) * mm});
            skLineSegment(sketch, "E131", {"start": v(-1, -9.15) * mm, "end": v(-1.48, -9) * mm, "construction": true});
            skCircle(sketch, "E132.cCircle", {"center": v(3.1, -9.52) * mm, "radius": 1.38 * mm, "construction": true});
            skLineSegment(sketch, "E132.0", {"start": v(4.71, -9) * mm, "end": v(4.1, -10.9) * mm});
            skLineSegment(sketch, "E132.1", {"start": v(4.1, -10.9) * mm, "end": v(2.1, -10.9) * mm});
            skLineSegment(sketch, "E132.2", {"start": v(2.1, -10.9) * mm, "end": v(1.48, -9) * mm});
            skLineSegment(sketch, "E132.3", {"start": v(1.48, -9) * mm, "end": v(3.1, -7.82) * mm});
            skLineSegment(sketch, "E132.4", {"start": v(3.1, -7.82) * mm, "end": v(4.71, -9) * mm});
            skPoint(sketch, "E132.0.midPoint", {"position": v(4.4, -9.95) * mm});
            skLineSegment(sketch, "E133", {"start": v(1.48, -9) * mm, "end": v(1, -9.15) * mm, "construction": true});
            skLineSegment(sketch, "E134", {"start": v(-8.1, -0.19) * mm, "end": v(-8.57, -1.63) * mm});
            skLineSegment(sketch, "E135", {"start": v(-8.57, -1.63) * mm, "end": v(-7.89, -3.72) * mm});
            skLineSegment(sketch, "E136", {"start": v(-7.89, -3.72) * mm, "end": v(-6.66, -4.6) * mm});
            skLineSegment(sketch, "E137", {"start": v(-6.66, -4.6) * mm, "end": v(-7.2, -2.97) * mm});
            skLineSegment(sketch, "E138", {"start": v(-7.2, -2.97) * mm, "end": v(-5.68, -1.88) * mm});
            skLineSegment(sketch, "E139", {"start": v(-5.68, -1.88) * mm, "end": v(-7.55, -1.88) * mm});
            skLineSegment(sketch, "E140", {"start": v(-7.55, -1.88) * mm, "end": v(-8.1, -0.19) * mm});
            skLineSegment(sketch, "E141", {"start": v(-2.32, -7.76) * mm, "end": v(-0.55, -7.76) * mm});
            skLineSegment(sketch, "E142", {"start": v(-0.55, -7.76) * mm, "end": v(0, -6.07) * mm});
            skLineSegment(sketch, "E143", {"start": v(0, -6.07) * mm, "end": v(0.55, -7.76) * mm});
            skLineSegment(sketch, "E144", {"start": v(0.55, -7.76) * mm, "end": v(2.32, -7.76) * mm});
            skLineSegment(sketch, "E145", {"start": v(2.32, -7.76) * mm, "end": v(1.1, -8.65) * mm});
            skLineSegment(sketch, "E146", {"start": v(1.1, -8.65) * mm, "end": v(-1.1, -8.65) * mm});
            skLineSegment(sketch, "E147", {"start": v(-1.1, -8.65) * mm, "end": v(-2.32, -7.76) * mm});
            skLineSegment(sketch, "E148", {"start": v(2.68, 7.64) * mm, "end": v(4.2, 7.64) * mm});
            skLineSegment(sketch, "E149", {"start": v(4.2, 7.64) * mm, "end": v(5.97, 6.35) * mm});
            skLineSegment(sketch, "E150", {"start": v(5.97, 6.35) * mm, "end": v(6.44, 4.91) * mm});
            skLineSegment(sketch, "E151", {"start": v(6.44, 4.91) * mm, "end": v(5, 5.96) * mm});
            skLineSegment(sketch, "E152", {"start": v(5, 5.96) * mm, "end": v(3.57, 4.91) * mm});
            skLineSegment(sketch, "E153", {"start": v(3.57, 4.91) * mm, "end": v(4.12, 6.6) * mm});
            skLineSegment(sketch, "E154", {"start": v(4.12, 6.6) * mm, "end": v(2.68, 7.64) * mm});
            skLineSegment(sketch, "E155", {"start": v(-6.44, 4.91) * mm, "end": v(-5.97, 6.35) * mm});
            skLineSegment(sketch, "E156", {"start": v(-5.97, 6.35) * mm, "end": v(-4.2, 7.64) * mm});
            skLineSegment(sketch, "E157", {"start": v(-4.2, 7.64) * mm, "end": v(-2.68, 7.64) * mm});
            skLineSegment(sketch, "E158", {"start": v(-2.68, 7.64) * mm, "end": v(-4.12, 6.6) * mm});
            skLineSegment(sketch, "E159", {"start": v(-4.12, 6.6) * mm, "end": v(-3.57, 4.91) * mm});
            skLineSegment(sketch, "E160", {"start": v(-3.57, 4.91) * mm, "end": v(-5, 5.96) * mm});
            skLineSegment(sketch, "E161", {"start": v(-5, 5.96) * mm, "end": v(-6.44, 4.91) * mm});
            skSolve(sketch);
        }
        {
            var Q0;
            Q0 = qSketchRegion(id + "F5", true);
            extrude(context, id + "F6", {"entities" : qUnion([Q0]), "operationType" : NewBodyOperationType.REMOVE, "endBound" : BoundingType.THROUGH_ALL, "oppositeDirection" : true, "depth" : 25 * mm, "offsetDistance" : 25 * mm});
        }
        {
            var Q0;
            Q0=makeQuery(id+"F1.opExtrude","CAP_FACE",FACE,{"disambiguationData":[OSD([sQuery(id+"F0.wireOp",EDGE,"E0")])],"isStart":false});
            var sketch = newSketch(context, id + "F7", { "sketchPlane" : qUnion([Q0])});
            skLineSegment(sketch, "E162", {"start": v(5.77, 10.4) * mm, "end": v(7.55, 10.4) * mm});
            skLineSegment(sketch, "E163", {"start": v(7.55, 10.4) * mm, "end": v(8.1, 8.7) * mm});
            skLineSegment(sketch, "E164", {"start": v(8.1, 8.7) * mm, "end": v(8.65, 10.4) * mm});
            skLineSegment(sketch, "E165", {"start": v(8.65, 10.4) * mm, "end": v(10.42, 10.4) * mm});
            skLineSegment(sketch, "E166", {"start": v(10.42, 10.4) * mm, "end": v(8.99, 11.44) * mm});
            skLineSegment(sketch, "E167", {"start": v(8.99, 11.44) * mm, "end": v(9.54, 13.12) * mm});
            skLineSegment(sketch, "E168", {"start": v(9.54, 13.12) * mm, "end": v(8.1, 12.08) * mm});
            skLineSegment(sketch, "E169", {"start": v(8.1, 12.08) * mm, "end": v(6.69, 13.1) * mm});
            skLineSegment(sketch, "E170", {"start": v(6.69, 13.1) * mm, "end": v(7.23, 11.45) * mm});
            skLineSegment(sketch, "E171", {"start": v(7.23, 11.45) * mm, "end": v(5.77, 10.4) * mm});
            skCircle(sketch, "E172.cCircle", {"center": v(10, 8.51) * mm, "radius": 1.38 * mm, "construction": true});
            skLineSegment(sketch, "E172.0", {"start": v(11.63, 7.99) * mm, "end": v(10, 6.81) * mm});
            skLineSegment(sketch, "E172.1", {"start": v(10, 6.81) * mm, "end": v(8.4, 7.99) * mm});
            skLineSegment(sketch, "E172.2", {"start": v(8.4, 7.99) * mm, "end": v(9, 9.9) * mm});
            skLineSegment(sketch, "E172.3", {"start": v(9, 9.9) * mm, "end": v(11, 9.9) * mm});
            skLineSegment(sketch, "E172.4", {"start": v(11, 9.9) * mm, "end": v(11.63, 7.99) * mm});
            skPoint(sketch, "E172.0.midPoint", {"position": v(10.82, 7.4) * mm});
            skLineSegment(sketch, "E173", {"start": v(8.4, 7.99) * mm, "end": v(8.1, 7.58) * mm, "construction": true});
            skCircle(sketch, "E174.cCircle", {"center": v(5, 12.17) * mm, "radius": 1.4 * mm, "construction": true});
            skLineSegment(sketch, "E174.0", {"start": v(6.01, 13.56) * mm, "end": v(6.64, 11.64) * mm});
            skLineSegment(sketch, "E174.1", {"start": v(6.64, 11.64) * mm, "end": v(5, 10.45) * mm});
            skLineSegment(sketch, "E174.2", {"start": v(5, 10.45) * mm, "end": v(3.37, 11.64) * mm});
            skLineSegment(sketch, "E174.3", {"start": v(3.37, 11.64) * mm, "end": v(4, 13.56) * mm});
            skLineSegment(sketch, "E174.4", {"start": v(4, 13.56) * mm, "end": v(6.01, 13.56) * mm});
            skPoint(sketch, "E174.0.midPoint", {"position": v(6.33, 12.6) * mm});
            skLineSegment(sketch, "E175", {"start": v(5, 10.45) * mm, "end": v(4.71, 10.05) * mm, "construction": true});
            skCircle(sketch, "E176.cCircle", {"center": v(13.1, 9.52) * mm, "radius": 1.38 * mm, "construction": true});
            skLineSegment(sketch, "E176.0", {"start": v(14.1, 8.14) * mm, "end": v(12.1, 8.14) * mm, "construction": true});
            skLineSegment(sketch, "E176.1", {"start": v(12.1, 8.14) * mm, "end": v(11.49, 10.05) * mm, "construction": true});
            skLineSegment(sketch, "E176.2", {"start": v(11.49, 10.05) * mm, "end": v(13.1, 11.22) * mm, "construction": true});
            skLineSegment(sketch, "E176.3", {"start": v(13.1, 11.22) * mm, "end": v(14.72, 10.05) * mm, "construction": true});
            skLineSegment(sketch, "E176.4", {"start": v(14.72, 10.05) * mm, "end": v(14.1, 8.14) * mm, "construction": true});
            skPoint(sketch, "E176.0.midPoint", {"position": v(13.1, 8.14) * mm});
            skCircle(sketch, "E177.cCircle", {"center": v(11.2, 12.15) * mm, "radius": 1.38 * mm, "construction": true});
            skLineSegment(sketch, "E177.0", {"start": v(12.81, 11.63) * mm, "end": v(11.2, 10.45) * mm, "construction": true});
            skLineSegment(sketch, "E177.1", {"start": v(11.2, 10.45) * mm, "end": v(9.57, 11.63) * mm, "construction": true});
            skLineSegment(sketch, "E177.2", {"start": v(9.57, 11.63) * mm, "end": v(10.2, 13.53) * mm, "construction": true});
            skLineSegment(sketch, "E177.3", {"start": v(10.2, 13.53) * mm, "end": v(12.2, 13.53) * mm, "construction": true});
            skLineSegment(sketch, "E177.4", {"start": v(12.2, 13.53) * mm, "end": v(12.81, 11.63) * mm, "construction": true});
            skPoint(sketch, "E177.0.midPoint", {"position": v(12, 11.04) * mm});
            skCircle(sketch, "E178.cCircle", {"center": v(11.2, 3.64) * mm, "radius": 1.38 * mm, "construction": true});
            skLineSegment(sketch, "E178.0", {"start": v(12.81, 4.16) * mm, "end": v(12.2, 2.26) * mm});
            skLineSegment(sketch, "E178.1", {"start": v(12.2, 2.26) * mm, "end": v(10.2, 2.26) * mm});
            skLineSegment(sketch, "E178.2", {"start": v(10.2, 2.26) * mm, "end": v(9.57, 4.16) * mm});
            skLineSegment(sketch, "E178.3", {"start": v(9.57, 4.16) * mm, "end": v(11.2, 5.34) * mm});
            skLineSegment(sketch, "E178.4", {"start": v(11.2, 5.34) * mm, "end": v(12.81, 4.16) * mm});
            skPoint(sketch, "E178.0.midPoint", {"position": v(12.5, 3.21) * mm});
            skLineSegment(sketch, "E179", {"start": v(9.1, 4) * mm, "end": v(9.57, 4.16) * mm, "construction": true});
            skLineSegment(sketch, "E180", {"start": v(9.75, 4.91) * mm, "end": v(10.22, 6.35) * mm});
            skLineSegment(sketch, "E181", {"start": v(10.22, 6.35) * mm, "end": v(11.45, 7.24) * mm});
            skLineSegment(sketch, "E182", {"start": v(11.45, 7.24) * mm, "end": v(10.98, 5.8) * mm});
            skLineSegment(sketch, "E183", {"start": v(10.98, 5.8) * mm, "end": v(9.75, 4.91) * mm});
            skCircle(sketch, "E184.cCircle", {"center": v(13.1, 6.27) * mm, "radius": 1.38 * mm, "construction": true});
            skLineSegment(sketch, "E184.0", {"start": v(14.1, 7.64) * mm, "end": v(14.72, 5.74) * mm});
            skLineSegment(sketch, "E184.1", {"start": v(14.72, 5.74) * mm, "end": v(13.1, 4.57) * mm});
            skLineSegment(sketch, "E184.2", {"start": v(13.1, 4.57) * mm, "end": v(11.49, 5.74) * mm});
            skLineSegment(sketch, "E184.3", {"start": v(11.49, 5.74) * mm, "end": v(12.1, 7.64) * mm});
            skLineSegment(sketch, "E184.4", {"start": v(12.1, 7.64) * mm, "end": v(14.1, 7.64) * mm});
            skPoint(sketch, "E184.0.midPoint", {"position": v(14.41, 6.7) * mm});
            skLineSegment(sketch, "E185", {"start": v(12.81, 4.16) * mm, "end": v(13.1, 4.57) * mm, "construction": true});
            skLineSegment(sketch, "E186", {"start": v(14.1, 8.14) * mm, "end": v(14.1, 7.64) * mm, "construction": true});
            skLineSegment(sketch, "E187", {"start": v(12.81, 11.63) * mm, "end": v(13.1, 11.22) * mm, "construction": true});
            skCircle(sketch, "E188.cCircle", {"center": v(11.2, 15.4) * mm, "radius": 1.38 * mm, "construction": true});
            skLineSegment(sketch, "E188.0", {"start": v(12.81, 15.93) * mm, "end": v(12.2, 14.03) * mm, "construction": true});
            skLineSegment(sketch, "E188.1", {"start": v(12.2, 14.03) * mm, "end": v(10.2, 14.03) * mm, "construction": true});
            skLineSegment(sketch, "E188.2", {"start": v(10.2, 14.03) * mm, "end": v(9.57, 15.93) * mm, "construction": true});
            skLineSegment(sketch, "E188.3", {"start": v(9.57, 15.93) * mm, "end": v(11.2, 17.1) * mm, "construction": true});
            skLineSegment(sketch, "E188.4", {"start": v(11.2, 17.1) * mm, "end": v(12.81, 15.93) * mm, "construction": true});
            skPoint(sketch, "E188.0.midPoint", {"position": v(12.5, 14.98) * mm});
            skLineSegment(sketch, "E189", {"start": v(12.2, 14.03) * mm, "end": v(12.2, 13.53) * mm, "construction": true});
            skCircle(sketch, "E190.cCircle", {"center": v(8.1, 14.4) * mm, "radius": 1.38 * mm, "construction": true});
            skLineSegment(sketch, "E190.0", {"start": v(9.1, 15.78) * mm, "end": v(9.72, 13.87) * mm, "construction": true});
            skLineSegment(sketch, "E190.1", {"start": v(9.72, 13.87) * mm, "end": v(8.1, 12.7) * mm, "construction": true});
            skLineSegment(sketch, "E190.2", {"start": v(8.1, 12.7) * mm, "end": v(6.48, 13.87) * mm, "construction": true});
            skLineSegment(sketch, "E190.3", {"start": v(6.48, 13.87) * mm, "end": v(7.1, 15.78) * mm, "construction": true});
            skLineSegment(sketch, "E190.4", {"start": v(7.1, 15.78) * mm, "end": v(9.1, 15.78) * mm, "construction": true});
            skPoint(sketch, "E190.0.midPoint", {"position": v(9.4, 14.83) * mm});
            skLineSegment(sketch, "E191", {"start": v(9.57, 15.93) * mm, "end": v(9.1, 15.78) * mm, "construction": true});
            skSolve(sketch);
        }
        {
            var Q0;
            Q0 = qSketchRegion(id + "F7", true);
            extrude(context, id + "F8", {"entities" : qUnion([Q0]), "operationType" : NewBodyOperationType.REMOVE, "endBound" : BoundingType.THROUGH_ALL, "oppositeDirection" : true, "depth" : 25 * mm, "offsetDistance" : 25 * mm});
        }
        {
            var Q0;
            Q0=makeQuery(id+"F1.opExtrude","CAP_FACE",FACE,{"disambiguationData":[OSD([sQuery(id+"F0.wireOp",EDGE,"E0")])],"isStart":false});
            var sketch = newSketch(context, id + "F9", { "sketchPlane" : qUnion([Q0])});
            skLineSegment(sketch, "E192", {"start": v(-8.1, 8.7) * mm, "end": v(-7.55, 10.4) * mm});
            skLineSegment(sketch, "E193", {"start": v(-7.55, 10.4) * mm, "end": v(-5.78, 10.4) * mm});
            skLineSegment(sketch, "E194", {"start": v(-5.78, 10.4) * mm, "end": v(-7.21, 11.43) * mm});
            skLineSegment(sketch, "E195", {"start": v(-7.21, 11.43) * mm, "end": v(-6.66, 13.12) * mm});
            skLineSegment(sketch, "E196", {"start": v(-6.66, 13.12) * mm, "end": v(-8.1, 12.08) * mm});
            skLineSegment(sketch, "E197", {"start": v(-8.1, 12.08) * mm, "end": v(-9.54, 13.12) * mm});
            skLineSegment(sketch, "E198", {"start": v(-9.54, 13.12) * mm, "end": v(-8.99, 11.43) * mm});
            skLineSegment(sketch, "E199", {"start": v(-8.99, 11.43) * mm, "end": v(-10.42, 10.4) * mm});
            skLineSegment(sketch, "E200", {"start": v(-10.42, 10.4) * mm, "end": v(-8.65, 10.4) * mm});
            skLineSegment(sketch, "E201", {"start": v(-8.65, 10.4) * mm, "end": v(-8.1, 8.7) * mm});
            skCircle(sketch, "E202.cCircle", {"center": v(-5, 12.15) * mm, "radius": 1.38 * mm, "construction": true});
            skLineSegment(sketch, "E202.0", {"start": v(-3.39, 11.63) * mm, "end": v(-5, 10.45) * mm});
            skLineSegment(sketch, "E202.1", {"start": v(-5, 10.45) * mm, "end": v(-6.62, 11.63) * mm});
            skLineSegment(sketch, "E202.2", {"start": v(-6.62, 11.63) * mm, "end": v(-6, 13.53) * mm});
            skLineSegment(sketch, "E202.3", {"start": v(-6, 13.53) * mm, "end": v(-4, 13.53) * mm});
            skLineSegment(sketch, "E202.4", {"start": v(-4, 13.53) * mm, "end": v(-3.39, 11.63) * mm});
            skPoint(sketch, "E202.0.midPoint", {"position": v(-4.2, 11.04) * mm});
            skCircle(sketch, "E203.cCircle", {"center": v(-10.01, 8.52) * mm, "radius": 1.38 * mm, "construction": true});
            skLineSegment(sketch, "E203.0", {"start": v(-8.4, 8) * mm, "end": v(-10.01, 6.81) * mm});
            skLineSegment(sketch, "E203.1", {"start": v(-10.01, 6.81) * mm, "end": v(-11.63, 8) * mm});
            skLineSegment(sketch, "E203.2", {"start": v(-11.63, 8) * mm, "end": v(-11.01, 9.9) * mm});
            skLineSegment(sketch, "E203.3", {"start": v(-11.01, 9.9) * mm, "end": v(-9.01, 9.9) * mm});
            skLineSegment(sketch, "E203.4", {"start": v(-9.01, 9.9) * mm, "end": v(-8.4, 8) * mm});
            skPoint(sketch, "E203.0.midPoint", {"position": v(-9.2, 7.4) * mm});
            skCircle(sketch, "E204.cCircle", {"center": v(0, 11.77) * mm, "radius": 1.38 * mm, "construction": true});
            skLineSegment(sketch, "E204.0", {"start": v(1, 10.4) * mm, "end": v(-1, 10.4) * mm});
            skLineSegment(sketch, "E204.1", {"start": v(-1, 10.4) * mm, "end": v(-1.62, 12.3) * mm});
            skLineSegment(sketch, "E204.2", {"start": v(-1.62, 12.3) * mm, "end": v(0, 13.47) * mm});
            skLineSegment(sketch, "E204.3", {"start": v(0, 13.47) * mm, "end": v(1.62, 12.3) * mm});
            skLineSegment(sketch, "E204.4", {"start": v(1.62, 12.3) * mm, "end": v(1, 10.4) * mm});
            skPoint(sketch, "E204.0.midPoint", {"position": v(0, 10.4) * mm});
            skLineSegment(sketch, "E205", {"start": v(1, 10.4) * mm, "end": v(1, 9.9) * mm, "construction": true});
            skLineSegment(sketch, "E206", {"start": v(-3.39, 11.63) * mm, "end": v(-3.1, 11.22) * mm, "construction": true});
            skLineSegment(sketch, "E207", {"start": v(-8.4, 8) * mm, "end": v(-8.1, 7.59) * mm, "construction": true});
            skCircle(sketch, "E208.cCircle", {"center": v(-5, 15.4) * mm, "radius": 1.38 * mm, "construction": true});
            skLineSegment(sketch, "E208.0", {"start": v(-3.39, 15.93) * mm, "end": v(-4, 14.03) * mm, "construction": true});
            skLineSegment(sketch, "E208.1", {"start": v(-4, 14.03) * mm, "end": v(-6, 14.03) * mm, "construction": true});
            skLineSegment(sketch, "E208.2", {"start": v(-6, 14.03) * mm, "end": v(-6.62, 15.93) * mm, "construction": true});
            skLineSegment(sketch, "E208.3", {"start": v(-6.62, 15.93) * mm, "end": v(-5, 17.1) * mm, "construction": true});
            skLineSegment(sketch, "E208.4", {"start": v(-5, 17.1) * mm, "end": v(-3.39, 15.93) * mm, "construction": true});
            skPoint(sketch, "E208.0.midPoint", {"position": v(-3.7, 14.98) * mm});
            skLineSegment(sketch, "E209", {"start": v(-4, 14.03) * mm, "end": v(-4, 13.53) * mm, "construction": true});
            skCircle(sketch, "E210.cCircle", {"center": v(-8.1, 14.4) * mm, "radius": 1.38 * mm, "construction": true});
            skLineSegment(sketch, "E210.0", {"start": v(-7.1, 15.78) * mm, "end": v(-6.48, 13.87) * mm, "construction": true});
            skLineSegment(sketch, "E210.1", {"start": v(-6.48, 13.87) * mm, "end": v(-8.1, 12.7) * mm, "construction": true});
            skLineSegment(sketch, "E210.2", {"start": v(-8.1, 12.7) * mm, "end": v(-9.72, 13.87) * mm, "construction": true});
            skLineSegment(sketch, "E210.3", {"start": v(-9.72, 13.87) * mm, "end": v(-9.1, 15.78) * mm, "construction": true});
            skLineSegment(sketch, "E210.4", {"start": v(-9.1, 15.78) * mm, "end": v(-7.1, 15.78) * mm, "construction": true});
            skPoint(sketch, "E210.0.midPoint", {"position": v(-6.8, 14.82) * mm});
            skLineSegment(sketch, "E211", {"start": v(-6.62, 15.93) * mm, "end": v(-7.1, 15.78) * mm, "construction": true});
            skCircle(sketch, "E212.cCircle", {"center": v(-11.2, 15.4) * mm, "radius": 1.38 * mm, "construction": true});
            skLineSegment(sketch, "E212.0", {"start": v(-9.58, 15.93) * mm, "end": v(-10.2, 14.03) * mm, "construction": true});
            skLineSegment(sketch, "E212.1", {"start": v(-10.2, 14.03) * mm, "end": v(-12.2, 14.03) * mm, "construction": true});
            skLineSegment(sketch, "E212.2", {"start": v(-12.2, 14.03) * mm, "end": v(-12.81, 15.93) * mm, "construction": true});
            skLineSegment(sketch, "E212.3", {"start": v(-12.81, 15.93) * mm, "end": v(-11.2, 17.1) * mm, "construction": true});
            skLineSegment(sketch, "E212.4", {"start": v(-11.2, 17.1) * mm, "end": v(-9.58, 15.93) * mm, "construction": true});
            skPoint(sketch, "E212.0.midPoint", {"position": v(-9.88, 14.98) * mm});
            skCircle(sketch, "E213.cCircle", {"center": v(-11.2, 12.15) * mm, "radius": 1.38 * mm, "construction": true});
            skLineSegment(sketch, "E213.0", {"start": v(-12.81, 11.63) * mm, "end": v(-12.2, 13.53) * mm, "construction": true});
            skLineSegment(sketch, "E213.1", {"start": v(-12.2, 13.53) * mm, "end": v(-10.2, 13.53) * mm, "construction": true});
            skLineSegment(sketch, "E213.2", {"start": v(-10.2, 13.53) * mm, "end": v(-9.58, 11.63) * mm, "construction": true});
            skLineSegment(sketch, "E213.3", {"start": v(-9.58, 11.63) * mm, "end": v(-11.2, 10.45) * mm, "construction": true});
            skLineSegment(sketch, "E213.4", {"start": v(-11.2, 10.45) * mm, "end": v(-12.81, 11.63) * mm, "construction": true});
            skPoint(sketch, "E213.0.midPoint", {"position": v(-12.5, 12.58) * mm});
            skLineSegment(sketch, "E214", {"start": v(-9.58, 15.93) * mm, "end": v(-9.1, 15.78) * mm, "construction": true});
            skLineSegment(sketch, "E215", {"start": v(-12.2, 13.53) * mm, "end": v(-12.2, 14.03) * mm, "construction": true});
            skSolve(sketch);
        }
        {
            var Q0;
            Q0 = qSketchRegion(id + "F9", true);
            extrude(context, id + "F10", {"entities" : qUnion([Q0]), "operationType" : NewBodyOperationType.REMOVE, "endBound" : BoundingType.THROUGH_ALL, "oppositeDirection" : true, "depth" : 25 * mm, "offsetDistance" : 25 * mm});
        }
        {
            var Q0;
            Q0=makeQuery(id+"F1.opExtrude","CAP_FACE",FACE,{"disambiguationData":[OSD([sQuery(id+"F0.wireOp",EDGE,"E0")])],"isStart":false});
            var sketch = newSketch(context, id + "F11", { "sketchPlane" : qUnion([Q0])});
            skLineSegment(sketch, "E216", {"start": v(-11.67, -2.28) * mm, "end": v(-12.22, -3.97) * mm});
            skLineSegment(sketch, "E217", {"start": v(-12.22, -3.97) * mm, "end": v(-10.78, -5.01) * mm});
            skLineSegment(sketch, "E218", {"start": v(-10.78, -5.01) * mm, "end": v(-12.56, -5.01) * mm});
            skLineSegment(sketch, "E219", {"start": v(-12.56, -5.01) * mm, "end": v(-13.16, -6.86) * mm});
            skLineSegment(sketch, "E220", {"start": v(-13.16, -6.86) * mm, "end": v(-13.76, -5.01) * mm});
            skLineSegment(sketch, "E221", {"start": v(-13.76, -5.01) * mm, "end": v(-15.53, -5.01) * mm});
            skLineSegment(sketch, "E222", {"start": v(-15.53, -5.01) * mm, "end": v(-14.1, -3.97) * mm});
            skLineSegment(sketch, "E223", {"start": v(-14.1, -3.97) * mm, "end": v(-14.68, -2.18) * mm});
            skLineSegment(sketch, "E224", {"start": v(-14.68, -2.18) * mm, "end": v(-13.1, -3.32) * mm});
            skLineSegment(sketch, "E225", {"start": v(-13.1, -3.32) * mm, "end": v(-11.67, -2.28) * mm});
            skCircle(sketch, "E226.cCircle", {"center": v(-13.1, -1) * mm, "radius": 1.38 * mm, "construction": true});
            skLineSegment(sketch, "E226.0", {"start": v(-14.1, 0.37) * mm, "end": v(-12.1, 0.37) * mm});
            skLineSegment(sketch, "E226.1", {"start": v(-12.1, 0.37) * mm, "end": v(-11.49, -1.53) * mm});
            skLineSegment(sketch, "E226.2", {"start": v(-11.49, -1.53) * mm, "end": v(-13.1, -2.7) * mm});
            skLineSegment(sketch, "E226.3", {"start": v(-13.1, -2.7) * mm, "end": v(-14.72, -1.53) * mm});
            skLineSegment(sketch, "E226.4", {"start": v(-14.72, -1.53) * mm, "end": v(-14.1, 0.37) * mm});
            skPoint(sketch, "E226.0.midPoint", {"position": v(-13.1, 0.37) * mm});
            skCircle(sketch, "E227.cCircle", {"center": v(-16.2, 0) * mm, "radius": 1.38 * mm, "construction": true});
            skLineSegment(sketch, "E227.0", {"start": v(-16.2, 1.7) * mm, "end": v(-14.58, 0.53) * mm, "construction": true});
            skLineSegment(sketch, "E227.1", {"start": v(-14.58, 0.53) * mm, "end": v(-15.2, -1.38) * mm, "construction": true});
            skLineSegment(sketch, "E227.2", {"start": v(-15.2, -1.38) * mm, "end": v(-17.2, -1.38) * mm, "construction": true});
            skLineSegment(sketch, "E227.3", {"start": v(-17.2, -1.38) * mm, "end": v(-17.82, 0.53) * mm, "construction": true});
            skLineSegment(sketch, "E227.4", {"start": v(-17.82, 0.53) * mm, "end": v(-16.2, 1.7) * mm, "construction": true});
            skPoint(sketch, "E227.0.midPoint", {"position": v(-15.39, 1.11) * mm});
            skCircle(sketch, "E228.cCircle", {"center": v(-19.3, -1) * mm, "radius": 1.38 * mm, "construction": true});
            skLineSegment(sketch, "E228.0", {"start": v(-17.67, -1.53) * mm, "end": v(-19.3, -2.7) * mm, "construction": true});
            skLineSegment(sketch, "E228.1", {"start": v(-19.3, -2.7) * mm, "end": v(-20.9, -1.53) * mm, "construction": true});
            skLineSegment(sketch, "E228.2", {"start": v(-20.9, -1.53) * mm, "end": v(-20.3, 0.37) * mm, "construction": true});
            skLineSegment(sketch, "E228.3", {"start": v(-20.3, 0.37) * mm, "end": v(-18.3, 0.37) * mm, "construction": true});
            skLineSegment(sketch, "E228.4", {"start": v(-18.3, 0.37) * mm, "end": v(-17.67, -1.53) * mm, "construction": true});
            skPoint(sketch, "E228.0.midPoint", {"position": v(-18.48, -2.12) * mm});
            skCircle(sketch, "E229.cCircle", {"center": v(-16.3, -3.25) * mm, "radius": 1.38 * mm, "construction": true});
            skLineSegment(sketch, "E229.0", {"start": v(-15.3, -1.88) * mm, "end": v(-14.69, -3.78) * mm, "construction": true});
            skLineSegment(sketch, "E229.1", {"start": v(-14.69, -3.78) * mm, "end": v(-16.3, -4.95) * mm, "construction": true});
            skLineSegment(sketch, "E229.2", {"start": v(-16.3, -4.95) * mm, "end": v(-17.92, -3.78) * mm, "construction": true});
            skLineSegment(sketch, "E229.3", {"start": v(-17.92, -3.78) * mm, "end": v(-17.3, -1.88) * mm, "construction": true});
            skLineSegment(sketch, "E229.4", {"start": v(-17.3, -1.88) * mm, "end": v(-15.3, -1.88) * mm, "construction": true});
            skPoint(sketch, "E229.0.midPoint", {"position": v(-15, -2.83) * mm});
            skCircle(sketch, "E230.cCircle", {"center": v(-11.2, -6.89) * mm, "radius": 1.38 * mm, "construction": true});
            skLineSegment(sketch, "E230.0", {"start": v(-11.2, -8.6) * mm, "end": v(-12.81, -7.42) * mm});
            skLineSegment(sketch, "E230.1", {"start": v(-12.81, -7.42) * mm, "end": v(-12.2, -5.51) * mm});
            skLineSegment(sketch, "E230.2", {"start": v(-12.2, -5.51) * mm, "end": v(-10.2, -5.51) * mm});
            skLineSegment(sketch, "E230.3", {"start": v(-10.2, -5.51) * mm, "end": v(-9.57, -7.42) * mm});
            skLineSegment(sketch, "E230.4", {"start": v(-9.57, -7.42) * mm, "end": v(-11.2, -8.6) * mm});
            skPoint(sketch, "E230.0.midPoint", {"position": v(-12, -8) * mm});
            skLineSegment(sketch, "E231", {"start": v(-11.63, 0.53) * mm, "end": v(-12.1, 0.37) * mm, "construction": true});
            skLineSegment(sketch, "E232", {"start": v(-14.1, 0.37) * mm, "end": v(-14.58, 0.53) * mm, "construction": true});
            skLineSegment(sketch, "E233", {"start": v(-17.82, 0.53) * mm, "end": v(-18.3, 0.37) * mm, "construction": true});
            skLineSegment(sketch, "E234", {"start": v(-17.3, -1.88) * mm, "end": v(-17.2, -1.38) * mm, "construction": true});
            skLineSegment(sketch, "E235", {"start": v(-9.57, -7.42) * mm, "end": v(-9.1, -7.26) * mm, "construction": true});
            skCircle(sketch, "E236.cCircle", {"center": v(-18.22, -5.88) * mm, "radius": 1.38 * mm, "construction": true});
            skLineSegment(sketch, "E236.0", {"start": v(-16.6, -5.36) * mm, "end": v(-17.22, -7.26) * mm, "construction": true});
            skLineSegment(sketch, "E236.1", {"start": v(-17.22, -7.26) * mm, "end": v(-19.22, -7.26) * mm, "construction": true});
            skLineSegment(sketch, "E236.2", {"start": v(-19.22, -7.26) * mm, "end": v(-19.83, -5.36) * mm, "construction": true});
            skLineSegment(sketch, "E236.3", {"start": v(-19.83, -5.36) * mm, "end": v(-18.22, -4.18) * mm, "construction": true});
            skLineSegment(sketch, "E236.4", {"start": v(-18.22, -4.18) * mm, "end": v(-16.6, -5.36) * mm, "construction": true});
            skPoint(sketch, "E236.0.midPoint", {"position": v(-16.9, -6.3) * mm});
            skCircle(sketch, "E237.cCircle", {"center": v(-15.12, -6.89) * mm, "radius": 1.38 * mm, "construction": true});
            skLineSegment(sketch, "E237.0", {"start": v(-13.5, -7.42) * mm, "end": v(-15.12, -8.6) * mm, "construction": true});
            skLineSegment(sketch, "E237.1", {"start": v(-15.12, -8.6) * mm, "end": v(-16.74, -7.42) * mm, "construction": true});
            skLineSegment(sketch, "E237.2", {"start": v(-16.74, -7.42) * mm, "end": v(-16.12, -5.51) * mm, "construction": true});
            skLineSegment(sketch, "E237.3", {"start": v(-16.12, -5.51) * mm, "end": v(-14.12, -5.51) * mm, "construction": true});
            skLineSegment(sketch, "E237.4", {"start": v(-14.12, -5.51) * mm, "end": v(-13.5, -7.42) * mm, "construction": true});
            skPoint(sketch, "E237.0.midPoint", {"position": v(-14.31, -8) * mm});
            skLineSegment(sketch, "E238", {"start": v(-18.22, -4.18) * mm, "end": v(-17.92, -3.78) * mm, "construction": true});
            skLineSegment(sketch, "E239", {"start": v(-16.74, -7.42) * mm, "end": v(-17.22, -7.26) * mm, "construction": true});
            skSolve(sketch);
        }
        {
            var Q0;
            Q0 = qSketchRegion(id + "F11", true);
            extrude(context, id + "F12", {"entities" : qUnion([Q0]), "operationType" : NewBodyOperationType.REMOVE, "endBound" : BoundingType.THROUGH_ALL, "oppositeDirection" : true, "depth" : 25 * mm, "offsetDistance" : 25 * mm});
        }
        {
            var Q0;
            Q0=makeQuery(id+"F1.opExtrude","CAP_FACE",FACE,{"disambiguationData":[OSD([sQuery(id+"F0.wireOp",EDGE,"E0")])],"isStart":false});
            var sketch = newSketch(context, id + "F13", { "sketchPlane" : qUnion([Q0])});
            skLineSegment(sketch, "E240", {"start": v(11.67, -2.28) * mm, "end": v(12.22, -3.97) * mm});
            skLineSegment(sketch, "E241", {"start": v(12.22, -3.97) * mm, "end": v(10.78, -5.01) * mm});
            skLineSegment(sketch, "E242", {"start": v(10.78, -5.01) * mm, "end": v(12.56, -5.01) * mm});
            skLineSegment(sketch, "E243", {"start": v(12.56, -5.01) * mm, "end": v(13.1, -6.7) * mm});
            skLineSegment(sketch, "E244", {"start": v(13.1, -6.7) * mm, "end": v(13.65, -5.01) * mm});
            skLineSegment(sketch, "E245", {"start": v(13.65, -5.01) * mm, "end": v(15.43, -5.01) * mm});
            skLineSegment(sketch, "E246", {"start": v(15.43, -5.01) * mm, "end": v(14, -3.97) * mm});
            skLineSegment(sketch, "E247", {"start": v(14, -3.97) * mm, "end": v(14.54, -2.28) * mm});
            skLineSegment(sketch, "E248", {"start": v(14.54, -2.28) * mm, "end": v(13.1, -3.32) * mm});
            skLineSegment(sketch, "E249", {"start": v(13.1, -3.32) * mm, "end": v(11.67, -2.28) * mm});
            skCircle(sketch, "E250.cCircle", {"center": v(13.1, -1) * mm, "radius": 1.38 * mm, "construction": true});
            skLineSegment(sketch, "E250.0", {"start": v(14.72, -1.53) * mm, "end": v(13.1, -2.7) * mm});
            skLineSegment(sketch, "E250.1", {"start": v(13.1, -2.7) * mm, "end": v(11.49, -1.53) * mm});
            skLineSegment(sketch, "E250.2", {"start": v(11.49, -1.53) * mm, "end": v(12.1, 0.37) * mm});
            skLineSegment(sketch, "E250.3", {"start": v(12.1, 0.37) * mm, "end": v(14.1, 0.37) * mm});
            skLineSegment(sketch, "E250.4", {"start": v(14.1, 0.37) * mm, "end": v(14.72, -1.53) * mm});
            skPoint(sketch, "E250.0.midPoint", {"position": v(13.91, -2.12) * mm});
            skCircle(sketch, "E251.cCircle", {"center": v(11.2, -6.89) * mm, "radius": 1.38 * mm, "construction": true});
            skLineSegment(sketch, "E251.0", {"start": v(12.2, -5.51) * mm, "end": v(12.81, -7.42) * mm});
            skLineSegment(sketch, "E251.1", {"start": v(12.81, -7.42) * mm, "end": v(11.2, -8.6) * mm});
            skLineSegment(sketch, "E251.2", {"start": v(11.2, -8.6) * mm, "end": v(9.57, -7.42) * mm});
            skLineSegment(sketch, "E251.3", {"start": v(9.57, -7.42) * mm, "end": v(10.2, -5.51) * mm});
            skLineSegment(sketch, "E251.4", {"start": v(10.2, -5.51) * mm, "end": v(12.2, -5.51) * mm});
            skPoint(sketch, "E251.0.midPoint", {"position": v(12.5, -6.46) * mm});
            skCircle(sketch, "E252.cCircle", {"center": v(16.2, 0) * mm, "radius": 1.38 * mm, "construction": true});
            skLineSegment(sketch, "E252.0", {"start": v(17.82, 0.53) * mm, "end": v(17.2, -1.38) * mm, "construction": true});
            skLineSegment(sketch, "E252.1", {"start": v(17.2, -1.38) * mm, "end": v(15.2, -1.38) * mm, "construction": true});
            skLineSegment(sketch, "E252.2", {"start": v(15.2, -1.38) * mm, "end": v(14.58, 0.53) * mm, "construction": true});
            skLineSegment(sketch, "E252.3", {"start": v(14.58, 0.53) * mm, "end": v(16.2, 1.7) * mm, "construction": true});
            skLineSegment(sketch, "E252.4", {"start": v(16.2, 1.7) * mm, "end": v(17.82, 0.53) * mm, "construction": true});
            skPoint(sketch, "E252.0.midPoint", {"position": v(17.5, -0.43) * mm});
            skCircle(sketch, "E253.cCircle", {"center": v(13.1, -9.52) * mm, "radius": 1.38 * mm, "construction": true});
            skLineSegment(sketch, "E253.0", {"start": v(14.1, -10.9) * mm, "end": v(12.1, -10.9) * mm, "construction": true});
            skLineSegment(sketch, "E253.1", {"start": v(12.1, -10.9) * mm, "end": v(11.49, -9) * mm, "construction": true});
            skLineSegment(sketch, "E253.2", {"start": v(11.49, -9) * mm, "end": v(13.1, -7.82) * mm, "construction": true});
            skLineSegment(sketch, "E253.3", {"start": v(13.1, -7.82) * mm, "end": v(14.72, -9) * mm, "construction": true});
            skLineSegment(sketch, "E253.4", {"start": v(14.72, -9) * mm, "end": v(14.1, -10.9) * mm, "construction": true});
            skPoint(sketch, "E253.0.midPoint", {"position": v(13.1, -10.9) * mm});
            skLineSegment(sketch, "E254", {"start": v(9.57, -7.42) * mm, "end": v(9.1, -7.26) * mm, "construction": true});
            skLineSegment(sketch, "E255", {"start": v(12.1, 0.37) * mm, "end": v(11.63, 0.53) * mm, "construction": true});
            skLineSegment(sketch, "E256", {"start": v(14.1, 0.37) * mm, "end": v(14.58, 0.53) * mm, "construction": true});
            skLineSegment(sketch, "E257", {"start": v(13.1, -7.82) * mm, "end": v(12.81, -7.42) * mm, "construction": true});
            skCircle(sketch, "E258.cCircle", {"center": v(15.02, -6.89) * mm, "radius": 1.38 * mm, "construction": true});
            skLineSegment(sketch, "E258.0", {"start": v(16.63, -7.42) * mm, "end": v(15.02, -8.6) * mm, "construction": true});
            skLineSegment(sketch, "E258.1", {"start": v(15.02, -8.6) * mm, "end": v(13.4, -7.42) * mm, "construction": true});
            skLineSegment(sketch, "E258.2", {"start": v(13.4, -7.42) * mm, "end": v(14.02, -5.51) * mm, "construction": true});
            skLineSegment(sketch, "E258.3", {"start": v(14.02, -5.51) * mm, "end": v(16.02, -5.51) * mm, "construction": true});
            skLineSegment(sketch, "E258.4", {"start": v(16.02, -5.51) * mm, "end": v(16.63, -7.42) * mm, "construction": true});
            skPoint(sketch, "E258.0.midPoint", {"position": v(15.83, -8) * mm});
            skLineSegment(sketch, "E259", {"start": v(13.4, -7.42) * mm, "end": v(13.1, -7.82) * mm, "construction": true});
            skCircle(sketch, "E260.cCircle", {"center": v(18.11, -5.88) * mm, "radius": 1.38 * mm, "construction": true});
            skLineSegment(sketch, "E260.0", {"start": v(19.11, -7.26) * mm, "end": v(17.11, -7.26) * mm, "construction": true});
            skLineSegment(sketch, "E260.1", {"start": v(17.11, -7.26) * mm, "end": v(16.5, -5.36) * mm, "construction": true});
            skLineSegment(sketch, "E260.2", {"start": v(16.5, -5.36) * mm, "end": v(18.11, -4.18) * mm, "construction": true});
            skLineSegment(sketch, "E260.3", {"start": v(18.11, -4.18) * mm, "end": v(19.73, -5.36) * mm, "construction": true});
            skLineSegment(sketch, "E260.4", {"start": v(19.73, -5.36) * mm, "end": v(19.11, -7.26) * mm, "construction": true});
            skPoint(sketch, "E260.0.midPoint", {"position": v(18.11, -7.26) * mm});
            skCircle(sketch, "E261.cCircle", {"center": v(16.2, -3.25) * mm, "radius": 1.38 * mm, "construction": true});
            skLineSegment(sketch, "E261.0", {"start": v(17.82, -3.78) * mm, "end": v(16.2, -4.95) * mm, "construction": true});
            skLineSegment(sketch, "E261.1", {"start": v(16.2, -4.95) * mm, "end": v(14.58, -3.78) * mm, "construction": true});
            skLineSegment(sketch, "E261.2", {"start": v(14.58, -3.78) * mm, "end": v(15.2, -1.88) * mm, "construction": true});
            skLineSegment(sketch, "E261.3", {"start": v(15.2, -1.88) * mm, "end": v(17.2, -1.88) * mm, "construction": true});
            skLineSegment(sketch, "E261.4", {"start": v(17.2, -1.88) * mm, "end": v(17.82, -3.78) * mm, "construction": true});
            skPoint(sketch, "E261.0.midPoint", {"position": v(17, -4.37) * mm});
            skLineSegment(sketch, "E262", {"start": v(16.63, -7.42) * mm, "end": v(17.11, -7.26) * mm, "construction": true});
            skLineSegment(sketch, "E263", {"start": v(18.11, -4.18) * mm, "end": v(17.82, -3.78) * mm, "construction": true});
            skSolve(sketch);
        }
        {
            var Q0;
            Q0 = qSketchRegion(id + "F13", true);
            extrude(context, id + "F14", {"entities" : qUnion([Q0]), "operationType" : NewBodyOperationType.REMOVE, "endBound" : BoundingType.THROUGH_ALL, "oppositeDirection" : true, "depth" : 25 * mm, "offsetDistance" : 25 * mm});
        }
        {
            var Q0;
            Q0=makeQuery(id+"F1.opExtrude","CAP_FACE",FACE,{"disambiguationData":[OSD([sQuery(id+"F0.wireOp",EDGE,"E0")])],"isStart":false});
            var sketch = newSketch(context, id + "F15", { "sketchPlane" : qUnion([Q0])});
            skLineSegment(sketch, "E264", {"start": v(-1.44, -11.8) * mm, "end": v(0, -12.85) * mm});
            skLineSegment(sketch, "E265", {"start": v(0, -12.85) * mm, "end": v(1.44, -11.8) * mm});
            skLineSegment(sketch, "E266", {"start": v(1.44, -11.8) * mm, "end": v(0.89, -13.5) * mm});
            skLineSegment(sketch, "E267", {"start": v(0.89, -13.5) * mm, "end": v(2.32, -14.53) * mm});
            skLineSegment(sketch, "E268", {"start": v(2.32, -14.53) * mm, "end": v(0.55, -14.53) * mm});
            skLineSegment(sketch, "E269", {"start": v(0.55, -14.53) * mm, "end": v(0, -16.22) * mm});
            skLineSegment(sketch, "E270", {"start": v(0, -16.22) * mm, "end": v(-0.55, -14.53) * mm});
            skLineSegment(sketch, "E271", {"start": v(-0.55, -14.53) * mm, "end": v(-2.32, -14.53) * mm});
            skLineSegment(sketch, "E272", {"start": v(-2.32, -14.53) * mm, "end": v(-0.89, -13.5) * mm});
            skLineSegment(sketch, "E273", {"start": v(-0.89, -13.5) * mm, "end": v(-1.44, -11.8) * mm});
            skCircle(sketch, "E274.cCircle", {"center": v(-3.1, -12.77) * mm, "radius": 1.38 * mm, "construction": true});
            skLineSegment(sketch, "E274.0", {"start": v(-2.1, -11.4) * mm, "end": v(-1.48, -13.3) * mm});
            skLineSegment(sketch, "E274.1", {"start": v(-1.48, -13.3) * mm, "end": v(-3.1, -14.48) * mm});
            skLineSegment(sketch, "E274.2", {"start": v(-3.1, -14.48) * mm, "end": v(-4.71, -13.3) * mm});
            skLineSegment(sketch, "E274.3", {"start": v(-4.71, -13.3) * mm, "end": v(-4.1, -11.4) * mm});
            skLineSegment(sketch, "E274.4", {"start": v(-4.1, -11.4) * mm, "end": v(-2.1, -11.4) * mm});
            skPoint(sketch, "E274.0.midPoint", {"position": v(-1.78, -12.35) * mm});
            skCircle(sketch, "E275.cCircle", {"center": v(3.1, -12.77) * mm, "radius": 1.38 * mm, "construction": true});
            skLineSegment(sketch, "E275.0", {"start": v(4.71, -13.3) * mm, "end": v(3.1, -14.48) * mm});
            skLineSegment(sketch, "E275.1", {"start": v(3.1, -14.48) * mm, "end": v(1.48, -13.3) * mm});
            skLineSegment(sketch, "E275.2", {"start": v(1.48, -13.3) * mm, "end": v(2.1, -11.4) * mm});
            skLineSegment(sketch, "E275.3", {"start": v(2.1, -11.4) * mm, "end": v(4.1, -11.4) * mm});
            skLineSegment(sketch, "E275.4", {"start": v(4.1, -11.4) * mm, "end": v(4.71, -13.3) * mm});
            skPoint(sketch, "E275.0.midPoint", {"position": v(3.9, -13.89) * mm});
            skLineSegment(sketch, "E276", {"start": v(4.1, -10.9) * mm, "end": v(4.1, -11.4) * mm, "construction": true});
            skLineSegment(sketch, "E277", {"start": v(-4.1, -10.9) * mm, "end": v(-4.1, -11.4) * mm, "construction": true});
            skCircle(sketch, "E278.cCircle", {"center": v(-5, -15.4) * mm, "radius": 1.38 * mm, "construction": true});
            skLineSegment(sketch, "E278.0", {"start": v(-3.39, -14.88) * mm, "end": v(-4, -16.78) * mm, "construction": true});
            skLineSegment(sketch, "E278.1", {"start": v(-4, -16.78) * mm, "end": v(-6, -16.78) * mm, "construction": true});
            skLineSegment(sketch, "E278.2", {"start": v(-6, -16.78) * mm, "end": v(-6.62, -14.88) * mm, "construction": true});
            skLineSegment(sketch, "E278.3", {"start": v(-6.62, -14.88) * mm, "end": v(-5, -13.7) * mm, "construction": true});
            skLineSegment(sketch, "E278.4", {"start": v(-5, -13.7) * mm, "end": v(-3.39, -14.88) * mm, "construction": true});
            skPoint(sketch, "E278.0.midPoint", {"position": v(-3.7, -15.83) * mm});
            skCircle(sketch, "E279.cCircle", {"center": v(5, -15.4) * mm, "radius": 1.38 * mm, "construction": true});
            skLineSegment(sketch, "E279.0", {"start": v(6.62, -14.88) * mm, "end": v(6, -16.78) * mm, "construction": true});
            skLineSegment(sketch, "E279.1", {"start": v(6, -16.78) * mm, "end": v(4, -16.78) * mm, "construction": true});
            skLineSegment(sketch, "E279.2", {"start": v(4, -16.78) * mm, "end": v(3.39, -14.88) * mm, "construction": true});
            skLineSegment(sketch, "E279.3", {"start": v(3.39, -14.88) * mm, "end": v(5, -13.7) * mm, "construction": true});
            skLineSegment(sketch, "E279.4", {"start": v(5, -13.7) * mm, "end": v(6.62, -14.88) * mm, "construction": true});
            skPoint(sketch, "E279.0.midPoint", {"position": v(6.31, -15.83) * mm});
            skCircle(sketch, "E280.cCircle", {"center": v(1.91, -16.41) * mm, "radius": 1.38 * mm, "construction": true});
            skLineSegment(sketch, "E280.0", {"start": v(3.53, -16.94) * mm, "end": v(1.91, -18.11) * mm, "construction": true});
            skLineSegment(sketch, "E280.1", {"start": v(1.91, -18.11) * mm, "end": v(0.3, -16.94) * mm, "construction": true});
            skLineSegment(sketch, "E280.2", {"start": v(0.3, -16.94) * mm, "end": v(0.91, -15.03) * mm, "construction": true});
            skLineSegment(sketch, "E280.3", {"start": v(0.91, -15.03) * mm, "end": v(2.91, -15.03) * mm, "construction": true});
            skLineSegment(sketch, "E280.4", {"start": v(2.91, -15.03) * mm, "end": v(3.53, -16.94) * mm, "construction": true});
            skPoint(sketch, "E280.0.midPoint", {"position": v(2.72, -17.52) * mm});
            skCircle(sketch, "E281.cCircle", {"center": v(-1.91, -16.41) * mm, "radius": 1.38 * mm, "construction": true});
            skLineSegment(sketch, "E281.0", {"start": v(-0.91, -15.03) * mm, "end": v(-0.3, -16.94) * mm, "construction": true});
            skLineSegment(sketch, "E281.1", {"start": v(-0.3, -16.94) * mm, "end": v(-1.91, -18.11) * mm, "construction": true});
            skLineSegment(sketch, "E281.2", {"start": v(-1.91, -18.11) * mm, "end": v(-3.53, -16.94) * mm, "construction": true});
            skLineSegment(sketch, "E281.3", {"start": v(-3.53, -16.94) * mm, "end": v(-2.91, -15.03) * mm, "construction": true});
            skLineSegment(sketch, "E281.4", {"start": v(-2.91, -15.03) * mm, "end": v(-0.91, -15.03) * mm, "construction": true});
            skPoint(sketch, "E281.0.midPoint", {"position": v(-0.6, -15.99) * mm});
            skLineSegment(sketch, "E282", {"start": v(4.71, -13.3) * mm, "end": v(5, -13.7) * mm, "construction": true});
            skLineSegment(sketch, "E283", {"start": v(3.53, -16.94) * mm, "end": v(4, -16.78) * mm, "construction": true});
            skLineSegment(sketch, "E284", {"start": v(-4.71, -13.3) * mm, "end": v(-5, -13.7) * mm, "construction": true});
            skLineSegment(sketch, "E285", {"start": v(-4, -16.78) * mm, "end": v(-3.53, -16.94) * mm, "construction": true});
            skSolve(sketch);
        }
        {
            var Q0;
            Q0 = qSketchRegion(id + "F15", true);
            extrude(context, id + "F16", {"entities" : qUnion([Q0]), "operationType" : NewBodyOperationType.REMOVE, "oppositeDirection" : true, "depth" : 25 * mm, "offsetDistance" : 25 * mm});
        }
        {
            var Q0;
            Q0=makeQuery(id+"F1.opExtrude","CAP_FACE",FACE,{"disambiguationData":[OSD([sQuery(id+"F0.wireOp",EDGE,"E0")])],"isStart":false});
            var sketch = newSketch(context, id + "F17", { "sketchPlane" : qUnion([Q0])});
            skCircle(sketch, "E286.cCircle", {"center": v(14.29, 2.63) * mm, "radius": 1.38 * mm, "construction": true});
            skLineSegment(sketch, "E286.0", {"start": v(15.29, 4) * mm, "end": v(15.9, 2.1) * mm});
            skLineSegment(sketch, "E286.1", {"start": v(15.9, 2.1) * mm, "end": v(14.29, 0.93) * mm});
            skLineSegment(sketch, "E286.2", {"start": v(14.29, 0.93) * mm, "end": v(12.67, 2.1) * mm});
            skLineSegment(sketch, "E286.3", {"start": v(12.67, 2.1) * mm, "end": v(13.29, 4) * mm});
            skLineSegment(sketch, "E286.4", {"start": v(13.29, 4) * mm, "end": v(15.29, 4) * mm});
            skPoint(sketch, "E286.0.midPoint", {"position": v(15.6, 3.06) * mm});
            skLineSegment(sketch, "E287", {"start": v(13.29, 4) * mm, "end": v(12.81, 4.16) * mm, "construction": true});
            skLineSegment(sketch, "E288", {"start": v(10.78, 1.76) * mm, "end": v(12.3, 1.76) * mm});
            skLineSegment(sketch, "E289", {"start": v(12.3, 1.76) * mm, "end": v(13.52, 0.87) * mm});
            skLineSegment(sketch, "E290", {"start": v(13.52, 0.87) * mm, "end": v(12, 0.87) * mm});
            skLineSegment(sketch, "E291", {"start": v(12, 0.87) * mm, "end": v(10.78, 1.76) * mm});
            skSolve(sketch);
        }
        {
            var Q0;
            Q0 = qSketchRegion(id + "F17", true);
            extrude(context, id + "F18", {"entities" : qUnion([Q0]), "operationType" : NewBodyOperationType.REMOVE, "endBound" : BoundingType.THROUGH_ALL, "oppositeDirection" : true, "depth" : 25 * mm, "offsetDistance" : 25 * mm});
        }
        {
            var Q0;
            Q0=makeQuery(id+"F1.opExtrude","CAP_FACE",FACE,{"disambiguationData":[OSD([sQuery(id+"F0.wireOp",EDGE,"E0")])],"isStart":false});
            var sketch = newSketch(context, id + "F19", { "sketchPlane" : qUnion([Q0])});
            skCircle(sketch, "E292.cCircle", {"center": v(6.92, -9.52) * mm, "radius": 1.38 * mm, "construction": true});
            skLineSegment(sketch, "E292.0", {"start": v(8.54, -9) * mm, "end": v(7.92, -10.9) * mm});
            skLineSegment(sketch, "E292.1", {"start": v(7.92, -10.9) * mm, "end": v(5.92, -10.9) * mm});
            skLineSegment(sketch, "E292.2", {"start": v(5.92, -10.9) * mm, "end": v(5.3, -9) * mm});
            skLineSegment(sketch, "E292.3", {"start": v(5.3, -9) * mm, "end": v(6.92, -7.82) * mm});
            skLineSegment(sketch, "E292.4", {"start": v(6.92, -7.82) * mm, "end": v(8.54, -9) * mm});
            skPoint(sketch, "E292.0.midPoint", {"position": v(8.23, -9.95) * mm});
            skCircle(sketch, "E293.cCircle", {"center": v(10.01, -10.53) * mm, "radius": 1.38 * mm, "construction": true});
            skLineSegment(sketch, "E293.0", {"start": v(10.01, -12.23) * mm, "end": v(8.4, -11.05) * mm});
            skLineSegment(sketch, "E293.1", {"start": v(8.4, -11.05) * mm, "end": v(9.01, -9.15) * mm});
            skLineSegment(sketch, "E293.2", {"start": v(9.01, -9.15) * mm, "end": v(11.01, -9.15) * mm});
            skLineSegment(sketch, "E293.3", {"start": v(11.01, -9.15) * mm, "end": v(11.63, -11.05) * mm});
            skLineSegment(sketch, "E293.4", {"start": v(11.63, -11.05) * mm, "end": v(10.01, -12.23) * mm});
            skPoint(sketch, "E293.0.midPoint", {"position": v(9.2, -11.64) * mm});
            skCircle(sketch, "E294.cCircle", {"center": v(6.92, -12.77) * mm, "radius": 1.38 * mm, "construction": true});
            skLineSegment(sketch, "E294.0", {"start": v(8.54, -13.3) * mm, "end": v(6.92, -14.48) * mm});
            skLineSegment(sketch, "E294.1", {"start": v(6.92, -14.48) * mm, "end": v(5.3, -13.3) * mm});
            skLineSegment(sketch, "E294.2", {"start": v(5.3, -13.3) * mm, "end": v(5.92, -11.4) * mm});
            skLineSegment(sketch, "E294.3", {"start": v(5.92, -11.4) * mm, "end": v(7.92, -11.4) * mm});
            skLineSegment(sketch, "E294.4", {"start": v(7.92, -11.4) * mm, "end": v(8.54, -13.3) * mm});
            skPoint(sketch, "E294.0.midPoint", {"position": v(7.73, -13.89) * mm});
            skLineSegment(sketch, "E295", {"start": v(5.3, -9) * mm, "end": v(5, -8.6) * mm, "construction": true});
            skLineSegment(sketch, "E296", {"start": v(11.63, -11.05) * mm, "end": v(12.1, -10.9) * mm, "construction": true});
            skLineSegment(sketch, "E297", {"start": v(6.62, -14.88) * mm, "end": v(6.92, -14.48) * mm, "construction": true});
            skLineSegment(sketch, "E298", {"start": v(7.69, -7.76) * mm, "end": v(9.2, -7.76) * mm});
            skLineSegment(sketch, "E299", {"start": v(9.2, -7.76) * mm, "end": v(10.42, -8.65) * mm});
            skLineSegment(sketch, "E300", {"start": v(10.42, -8.65) * mm, "end": v(8.91, -8.65) * mm});
            skLineSegment(sketch, "E301", {"start": v(8.91, -8.65) * mm, "end": v(7.69, -7.76) * mm});
            skLineSegment(sketch, "E302", {"start": v(5, -9.7) * mm, "end": v(4.54, -11.15) * mm});
            skLineSegment(sketch, "E303", {"start": v(4.54, -11.15) * mm, "end": v(5, -12.59) * mm});
            skLineSegment(sketch, "E304", {"start": v(5, -12.59) * mm, "end": v(5.47, -11.15) * mm});
            skLineSegment(sketch, "E305", {"start": v(5.47, -11.15) * mm, "end": v(5, -9.7) * mm});
            skSolve(sketch);
        }
        {
            var Q0;
            Q0 = qSketchRegion(id + "F19", true);
            extrude(context, id + "F20", {"entities" : qUnion([Q0]), "operationType" : NewBodyOperationType.REMOVE, "endBound" : BoundingType.THROUGH_ALL, "oppositeDirection" : true, "depth" : 25 * mm, "offsetDistance" : 25 * mm});
        }
        {
            var Q0;
            Q0=makeQuery(id+"F11.imprint","IMPRINT",FACE,{"disambiguationData":[TD([[makeQuery(id+"F11.imprint","IMPRINT",EDGE,{"derivedFrom":sQuery(id+"F11.wireOp",EDGE,"E216")}),1.0]])]});
            var sketch = newSketch(context, id + "F21", { "sketchPlane" : qUnion([Q0])});
            skCircle(sketch, "E306.cCircle", {"center": v(-6.92, -9.52) * mm, "radius": 1.38 * mm, "construction": true});
            skLineSegment(sketch, "E306.0", {"start": v(-7.92, -10.9) * mm, "end": v(-8.54, -9) * mm});
            skLineSegment(sketch, "E306.1", {"start": v(-8.54, -9) * mm, "end": v(-6.92, -7.82) * mm});
            skLineSegment(sketch, "E306.2", {"start": v(-6.92, -7.82) * mm, "end": v(-5.3, -9) * mm});
            skLineSegment(sketch, "E306.3", {"start": v(-5.3, -9) * mm, "end": v(-5.92, -10.9) * mm});
            skLineSegment(sketch, "E306.4", {"start": v(-5.92, -10.9) * mm, "end": v(-7.92, -10.9) * mm});
            skPoint(sketch, "E306.0.midPoint", {"position": v(-8.23, -9.95) * mm});
            skLineSegment(sketch, "E307", {"start": v(-5.3, -9) * mm, "end": v(-5, -8.6) * mm, "construction": true});
            skCircle(sketch, "E308.cCircle", {"center": v(-6.92, -12.77) * mm, "radius": 1.38 * mm, "construction": true});
            skLineSegment(sketch, "E308.0", {"start": v(-5.92, -11.4) * mm, "end": v(-5.3, -13.3) * mm});
            skLineSegment(sketch, "E308.1", {"start": v(-5.3, -13.3) * mm, "end": v(-6.92, -14.48) * mm});
            skLineSegment(sketch, "E308.2", {"start": v(-6.92, -14.48) * mm, "end": v(-8.54, -13.3) * mm});
            skLineSegment(sketch, "E308.3", {"start": v(-8.54, -13.3) * mm, "end": v(-7.92, -11.4) * mm});
            skLineSegment(sketch, "E308.4", {"start": v(-7.92, -11.4) * mm, "end": v(-5.92, -11.4) * mm});
            skPoint(sketch, "E308.0.midPoint", {"position": v(-5.6, -12.35) * mm});
            skLineSegment(sketch, "E309", {"start": v(-6.92, -14.48) * mm, "end": v(-6.62, -14.88) * mm, "construction": true});
            skCircle(sketch, "E310.cCircle", {"center": v(-13.2, -9.52) * mm, "radius": 1.38 * mm, "construction": true});
            skLineSegment(sketch, "E310.0", {"start": v(-14.2, -10.9) * mm, "end": v(-14.83, -9) * mm, "construction": true});
            skLineSegment(sketch, "E310.1", {"start": v(-14.83, -9) * mm, "end": v(-13.2, -7.82) * mm, "construction": true});
            skLineSegment(sketch, "E310.2", {"start": v(-13.2, -7.82) * mm, "end": v(-11.6, -9) * mm, "construction": true});
            skLineSegment(sketch, "E310.3", {"start": v(-11.6, -9) * mm, "end": v(-12.2, -10.9) * mm, "construction": true});
            skLineSegment(sketch, "E310.4", {"start": v(-12.2, -10.9) * mm, "end": v(-14.2, -10.9) * mm, "construction": true});
            skPoint(sketch, "E310.0.midPoint", {"position": v(-14.52, -9.95) * mm});
            skLineSegment(sketch, "E311", {"start": v(-14.83, -9) * mm, "end": v(-15.12, -8.6) * mm, "construction": true});
            skCircle(sketch, "E312.cCircle", {"center": v(-10.12, -10.53) * mm, "radius": 1.38 * mm, "construction": true});
            skLineSegment(sketch, "E312.0", {"start": v(-8.5, -11.05) * mm, "end": v(-10.12, -12.23) * mm});
            skLineSegment(sketch, "E312.1", {"start": v(-10.12, -12.23) * mm, "end": v(-11.73, -11.05) * mm});
            skLineSegment(sketch, "E312.2", {"start": v(-11.73, -11.05) * mm, "end": v(-11.12, -9.15) * mm});
            skLineSegment(sketch, "E312.3", {"start": v(-11.12, -9.15) * mm, "end": v(-9.12, -9.15) * mm});
            skLineSegment(sketch, "E312.4", {"start": v(-9.12, -9.15) * mm, "end": v(-8.5, -11.05) * mm});
            skPoint(sketch, "E312.0.midPoint", {"position": v(-9.3, -11.64) * mm});
            skLineSegment(sketch, "E313", {"start": v(-11.73, -11.05) * mm, "end": v(-12.2, -10.9) * mm, "construction": true});
            skLineSegment(sketch, "E314", {"start": v(-10.42, -8.65) * mm, "end": v(-8.91, -8.65) * mm});
            skLineSegment(sketch, "E315", {"start": v(-8.91, -8.65) * mm, "end": v(-7.69, -7.76) * mm});
            skLineSegment(sketch, "E316", {"start": v(-7.69, -7.76) * mm, "end": v(-9.2, -7.76) * mm});
            skLineSegment(sketch, "E317", {"start": v(-9.2, -7.76) * mm, "end": v(-10.42, -8.65) * mm});
            skLineSegment(sketch, "E318", {"start": v(-5, -9.7) * mm, "end": v(-5.47, -11.15) * mm});
            skLineSegment(sketch, "E319", {"start": v(-5.47, -11.15) * mm, "end": v(-5, -12.59) * mm});
            skLineSegment(sketch, "E320", {"start": v(-5, -12.59) * mm, "end": v(-4.54, -11.15) * mm});
            skLineSegment(sketch, "E321", {"start": v(-4.54, -11.15) * mm, "end": v(-5, -9.7) * mm});
            skSolve(sketch);
        }
        {
            var Q0;
            Q0 = qSketchRegion(id + "F21", true);
            extrude(context, id + "F22", {"entities" : qUnion([Q0]), "operationType" : NewBodyOperationType.REMOVE, "endBound" : BoundingType.THROUGH_ALL, "oppositeDirection" : true, "depth" : 25 * mm, "offsetDistance" : 25 * mm});
        }
        {
            var Q0;
            Q0=makeQuery(id+"F11.imprint","IMPRINT",FACE,{"disambiguationData":[TD([[makeQuery(id+"F11.imprint","IMPRINT",EDGE,{"derivedFrom":sQuery(id+"F11.wireOp",EDGE,"E216")}),1.0]])]});
            var sketch = newSketch(context, id + "F23", { "sketchPlane" : qUnion([Q0])});
            skCircle(sketch, "E322.cCircle", {"center": v(5, 15.4) * mm, "radius": 1.38 * mm, "construction": true});
            skLineSegment(sketch, "E322.0", {"start": v(6, 14.03) * mm, "end": v(4, 14.03) * mm, "construction": true});
            skLineSegment(sketch, "E322.1", {"start": v(4, 14.03) * mm, "end": v(3.39, 15.93) * mm, "construction": true});
            skLineSegment(sketch, "E322.2", {"start": v(3.39, 15.93) * mm, "end": v(5, 17.1) * mm, "construction": true});
            skLineSegment(sketch, "E322.3", {"start": v(5, 17.1) * mm, "end": v(6.62, 15.93) * mm, "construction": true});
            skLineSegment(sketch, "E322.4", {"start": v(6.62, 15.93) * mm, "end": v(6, 14.03) * mm, "construction": true});
            skPoint(sketch, "E322.0.midPoint", {"position": v(5, 14.03) * mm});
            skCircle(sketch, "E323.cCircle", {"center": v(1.91, 14.4) * mm, "radius": 1.38 * mm, "construction": true});
            skLineSegment(sketch, "E323.0", {"start": v(0.3, 13.87) * mm, "end": v(0.91, 15.78) * mm});
            skLineSegment(sketch, "E323.1", {"start": v(0.91, 15.78) * mm, "end": v(2.91, 15.78) * mm});
            skLineSegment(sketch, "E323.2", {"start": v(2.91, 15.78) * mm, "end": v(3.53, 13.87) * mm});
            skLineSegment(sketch, "E323.3", {"start": v(3.53, 13.87) * mm, "end": v(1.91, 12.7) * mm});
            skLineSegment(sketch, "E323.4", {"start": v(1.91, 12.7) * mm, "end": v(0.3, 13.87) * mm});
            skPoint(sketch, "E323.0.midPoint", {"position": v(0.6, 14.82) * mm});
            skCircle(sketch, "E324.cCircle", {"center": v(-1.91, 14.4) * mm, "radius": 1.38 * mm, "construction": true});
            skLineSegment(sketch, "E324.0", {"start": v(-0.3, 13.87) * mm, "end": v(-1.91, 12.7) * mm});
            skLineSegment(sketch, "E324.1", {"start": v(-1.91, 12.7) * mm, "end": v(-3.53, 13.87) * mm});
            skLineSegment(sketch, "E324.2", {"start": v(-3.53, 13.87) * mm, "end": v(-2.91, 15.78) * mm});
            skLineSegment(sketch, "E324.3", {"start": v(-2.91, 15.78) * mm, "end": v(-0.91, 15.78) * mm});
            skLineSegment(sketch, "E324.4", {"start": v(-0.91, 15.78) * mm, "end": v(-0.3, 13.87) * mm});
            skPoint(sketch, "E324.0.midPoint", {"position": v(-1.1, 13.29) * mm});
            skLineSegment(sketch, "E325", {"start": v(6, 14.03) * mm, "end": v(6.48, 13.87) * mm, "construction": true});
            skLineSegment(sketch, "E326", {"start": v(1.91, 12.7) * mm, "end": v(1.62, 12.3) * mm, "construction": true});
            skLineSegment(sketch, "E327", {"start": v(-2.91, 15.78) * mm, "end": v(-3.39, 15.93) * mm, "construction": true});
            skLineSegment(sketch, "E328", {"start": v(1.66, 10.8) * mm, "end": v(2.12, 12.23) * mm});
            skLineSegment(sketch, "E329", {"start": v(2.12, 12.23) * mm, "end": v(3.32, 13.1) * mm});
            skLineSegment(sketch, "E330", {"start": v(3.32, 13.1) * mm, "end": v(2.85, 11.66) * mm});
            skLineSegment(sketch, "E331", {"start": v(2.85, 11.66) * mm, "end": v(1.66, 10.8) * mm});
            skLineSegment(sketch, "E332", {"start": v(-1.66, 10.8) * mm, "end": v(-2.13, 12.23) * mm});
            skLineSegment(sketch, "E333", {"start": v(-2.13, 12.23) * mm, "end": v(-3.35, 13.12) * mm});
            skLineSegment(sketch, "E334", {"start": v(-3.35, 13.12) * mm, "end": v(-2.88, 11.68) * mm});
            skLineSegment(sketch, "E335", {"start": v(-2.88, 11.68) * mm, "end": v(-1.66, 10.8) * mm});
            skSolve(sketch);
        }
        {
            var Q0;
            Q0 = qSketchRegion(id + "F23", true);
            extrude(context, id + "F24", {"entities" : qUnion([Q0]), "operationType" : NewBodyOperationType.REMOVE, "endBound" : BoundingType.THROUGH_ALL, "oppositeDirection" : true, "depth" : 25 * mm, "offsetDistance" : 25 * mm});
        }
        {
            var Q0;
            Q0=makeQuery(id+"F11.imprint","IMPRINT",FACE,{"disambiguationData":[TD([[makeQuery(id+"F11.imprint","IMPRINT",EDGE,{"derivedFrom":sQuery(id+"F11.wireOp",EDGE,"E216")}),1.0]])]});
            var sketch = newSketch(context, id + "F25", { "sketchPlane" : qUnion([Q0])});
            skCircle(sketch, "E336.cCircle", {"center": v(-11.2, 3.64) * mm, "radius": 1.38 * mm, "construction": true});
            skLineSegment(sketch, "E336.0", {"start": v(-9.57, 4.16) * mm, "end": v(-10.2, 2.26) * mm});
            skLineSegment(sketch, "E336.1", {"start": v(-10.2, 2.26) * mm, "end": v(-12.2, 2.26) * mm});
            skLineSegment(sketch, "E336.2", {"start": v(-12.2, 2.26) * mm, "end": v(-12.81, 4.16) * mm});
            skLineSegment(sketch, "E336.3", {"start": v(-12.81, 4.16) * mm, "end": v(-11.2, 5.34) * mm});
            skLineSegment(sketch, "E336.4", {"start": v(-11.2, 5.34) * mm, "end": v(-9.57, 4.16) * mm});
            skPoint(sketch, "E336.0.midPoint", {"position": v(-9.88, 3.21) * mm});
            skCircle(sketch, "E337.cCircle", {"center": v(-14.29, 2.63) * mm, "radius": 1.38 * mm, "construction": true});
            skLineSegment(sketch, "E337.0", {"start": v(-12.67, 2.1) * mm, "end": v(-14.29, 0.93) * mm});
            skLineSegment(sketch, "E337.1", {"start": v(-14.29, 0.93) * mm, "end": v(-15.9, 2.1) * mm});
            skLineSegment(sketch, "E337.2", {"start": v(-15.9, 2.1) * mm, "end": v(-15.29, 4) * mm});
            skLineSegment(sketch, "E337.3", {"start": v(-15.29, 4) * mm, "end": v(-13.29, 4) * mm});
            skLineSegment(sketch, "E337.4", {"start": v(-13.29, 4) * mm, "end": v(-12.67, 2.1) * mm});
            skPoint(sketch, "E337.0.midPoint", {"position": v(-13.48, 1.52) * mm});
            skCircle(sketch, "E338.cCircle", {"center": v(-13.1, 9.52) * mm, "radius": 1.38 * mm, "construction": true});
            skLineSegment(sketch, "E338.0", {"start": v(-11.49, 10.05) * mm, "end": v(-12.1, 8.14) * mm, "construction": true});
            skLineSegment(sketch, "E338.1", {"start": v(-12.1, 8.14) * mm, "end": v(-14.1, 8.14) * mm, "construction": true});
            skLineSegment(sketch, "E338.2", {"start": v(-14.1, 8.14) * mm, "end": v(-14.72, 10.05) * mm, "construction": true});
            skLineSegment(sketch, "E338.3", {"start": v(-14.72, 10.05) * mm, "end": v(-13.1, 11.22) * mm, "construction": true});
            skLineSegment(sketch, "E338.4", {"start": v(-13.1, 11.22) * mm, "end": v(-11.49, 10.05) * mm, "construction": true});
            skPoint(sketch, "E338.0.midPoint", {"position": v(-11.8, 9.1) * mm});
            skCircle(sketch, "E339.cCircle", {"center": v(-13.1, 6.27) * mm, "radius": 1.38 * mm, "construction": true});
            skLineSegment(sketch, "E339.0", {"start": v(-11.49, 5.74) * mm, "end": v(-13.1, 4.57) * mm});
            skLineSegment(sketch, "E339.1", {"start": v(-13.1, 4.57) * mm, "end": v(-14.72, 5.74) * mm});
            skLineSegment(sketch, "E339.2", {"start": v(-14.72, 5.74) * mm, "end": v(-14.1, 7.64) * mm});
            skLineSegment(sketch, "E339.3", {"start": v(-14.1, 7.64) * mm, "end": v(-12.1, 7.64) * mm});
            skLineSegment(sketch, "E339.4", {"start": v(-12.1, 7.64) * mm, "end": v(-11.49, 5.74) * mm});
            skPoint(sketch, "E339.0.midPoint", {"position": v(-12.3, 5.15) * mm});
            skLineSegment(sketch, "E340", {"start": v(-9.57, 4.16) * mm, "end": v(-9.1, 4) * mm, "construction": true});
            skLineSegment(sketch, "E341", {"start": v(-15.9, 2.1) * mm, "end": v(-16.2, 1.7) * mm, "construction": true});
            skLineSegment(sketch, "E342", {"start": v(-13.1, 11.22) * mm, "end": v(-12.81, 11.63) * mm, "construction": true});
            skLineSegment(sketch, "E343", {"start": v(-14.1, 7.64) * mm, "end": v(-14.1, 8.14) * mm, "construction": true});
            skLineSegment(sketch, "E344", {"start": v(-13.52, 0.87) * mm, "end": v(-12.3, 1.76) * mm});
            skLineSegment(sketch, "E345", {"start": v(-12.3, 1.76) * mm, "end": v(-10.78, 1.76) * mm});
            skLineSegment(sketch, "E346", {"start": v(-10.78, 1.76) * mm, "end": v(-12, 0.87) * mm});
            skLineSegment(sketch, "E347", {"start": v(-12, 0.87) * mm, "end": v(-13.52, 0.87) * mm});
            skLineSegment(sketch, "E348", {"start": v(-11.45, 7.24) * mm, "end": v(-10.22, 6.35) * mm});
            skLineSegment(sketch, "E349", {"start": v(-10.22, 6.35) * mm, "end": v(-9.76, 4.91) * mm});
            skLineSegment(sketch, "E350", {"start": v(-9.76, 4.91) * mm, "end": v(-10.98, 5.8) * mm});
            skLineSegment(sketch, "E351", {"start": v(-10.98, 5.8) * mm, "end": v(-11.45, 7.24) * mm});
            skSolve(sketch);
        }
        {
            var Q0;
            Q0 = qSketchRegion(id + "F25", true);
            extrude(context, id + "F26", {"entities" : qUnion([Q0]), "operationType" : NewBodyOperationType.REMOVE, "endBound" : BoundingType.THROUGH_ALL, "oppositeDirection" : true, "depth" : 25 * mm, "offsetDistance" : 25 * mm});
        }
        {
            var Q0;
            Q0=makeQuery(id+"F1.opExtrude","CAP_FACE",FACE,{"disambiguationData":[OSD([sQuery(id+"F0.wireOp",EDGE,"E0"),sQuery(id+"F0.wireOp",EDGE,"E1.bottom"),sQuery(id+"F0.wireOp",EDGE,"E1.left"),sQuery(id+"F0.wireOp",EDGE,"E1.right")])],"isStart":false});
            var sketch = newSketch(context, id + "F27", { "sketchPlane" : qUnion([Q0])});
            skLineSegment(sketch, "E352.bottom", {"start": v(1.5, -21.32) * mm, "end": v(-1.5, -21.32) * mm});
            skLineSegment(sketch, "E352.top", {"start": v(1.5, -18.32) * mm, "end": v(-1.5, -18.32) * mm});
            skLineSegment(sketch, "E352.left", {"start": v(1.5, -21.32) * mm, "end": v(1.5, -18.32) * mm});
            skLineSegment(sketch, "E352.right", {"start": v(-1.5, -21.32) * mm, "end": v(-1.5, -18.32) * mm});
            skSolve(sketch);
        }
        {
            var Q0;
            Q0 = qSketchRegion(id + "F27", true);
            extrude(context, id + "F28", {"entities" : qUnion([Q0]), "operationType" : NewBodyOperationType.REMOVE, "endBound" : BoundingType.THROUGH_ALL, "oppositeDirection" : true, "depth" : 25 * mm, "offsetDistance" : 25 * mm});
        }
        {
            var Q0;
            Q0=makeQuery(id+"F28.boolean.opBoolean","COPY",EDGE,{"derivedFrom":makeQuery(id+"F28.opExtrude","SWEPT_EDGE",EDGE,{"disambiguationData":[OSD([sQuery(id+"F27.wireOp",EDGE,"E352.bottom"),sQuery(id+"F27.wireOp",EDGE,"E352.left")])]})});
            var Q1;
            Q1=makeQuery(id+"F28.boolean.opBoolean","COPY",EDGE,{"derivedFrom":makeQuery(id+"F28.opExtrude","SWEPT_EDGE",EDGE,{"disambiguationData":[OSD([sQuery(id+"F27.wireOp",EDGE,"E352.bottom"),sQuery(id+"F27.wireOp",EDGE,"E352.right")])]})});
            var Q2;
            Q2=makeQuery(id+"F28.boolean.opBoolean","COPY",EDGE,{"derivedFrom":makeQuery(id+"F28.opExtrude","SWEPT_EDGE",EDGE,{"disambiguationData":[OSD([sQuery(id+"F27.wireOp",EDGE,"E352.top"),sQuery(id+"F27.wireOp",EDGE,"E352.right")])]})});
            var Q3;
            Q3=makeQuery(id+"F28.boolean.opBoolean","COPY",EDGE,{"derivedFrom":makeQuery(id+"F28.opExtrude","SWEPT_EDGE",EDGE,{"disambiguationData":[OSD([sQuery(id+"F27.wireOp",EDGE,"E352.top"),sQuery(id+"F27.wireOp",EDGE,"E352.left")])]})});
            fillet(context, id + "F29", {"entities" : qUnion([Q0, Q1, Q2, Q3]), "radius" : 1 * mm, "tangentPropagation" : true, "allowEdgeOverflow" : false});
        }
        {
            var Q0;
            Q0=makeQuery(id+"F1.opExtrude","CAP_EDGE",EDGE,{"disambiguationData":[OSD([sQuery(id+"F0.wireOp",EDGE,"E1.left")])],"isStart":true});
            var Q1;
            Q1=makeQuery(id+"F1.opExtrude","CAP_EDGE",EDGE,{"disambiguationData":[OSD([sQuery(id+"F0.wireOp",EDGE,"E1.left")])],"isStart":false});
            var Q2;
            Q2=makeQuery(id+"F1.opExtrude","CAP_EDGE",EDGE,{"disambiguationData":[OSD([sQuery(id+"F0.wireOp",EDGE,"E1.right")])],"isStart":false});
            var Q3;
            Q3=makeQuery(id+"F1.opExtrude","CAP_EDGE",EDGE,{"disambiguationData":[OSD([sQuery(id+"F0.wireOp",EDGE,"E1.bottom")])],"isStart":false});
            var Q4;
            Q4=makeQuery(id+"F1.opExtrude","CAP_EDGE",EDGE,{"disambiguationData":[OSD([sQuery(id+"F0.wireOp",EDGE,"E1.bottom")])],"isStart":true});
            var Q5;
            Q5=makeQuery(id+"F1.opExtrude","CAP_EDGE",EDGE,{"disambiguationData":[OSD([sQuery(id+"F0.wireOp",EDGE,"E1.right")])],"isStart":true});
            fillet(context, id + "F30", {"entities" : qUnion([Q0, Q1, Q2, Q3, Q4, Q5]), "radius" : 0.5 * mm, "tangentPropagation" : true, "allowEdgeOverflow" : false});
        }
    });
